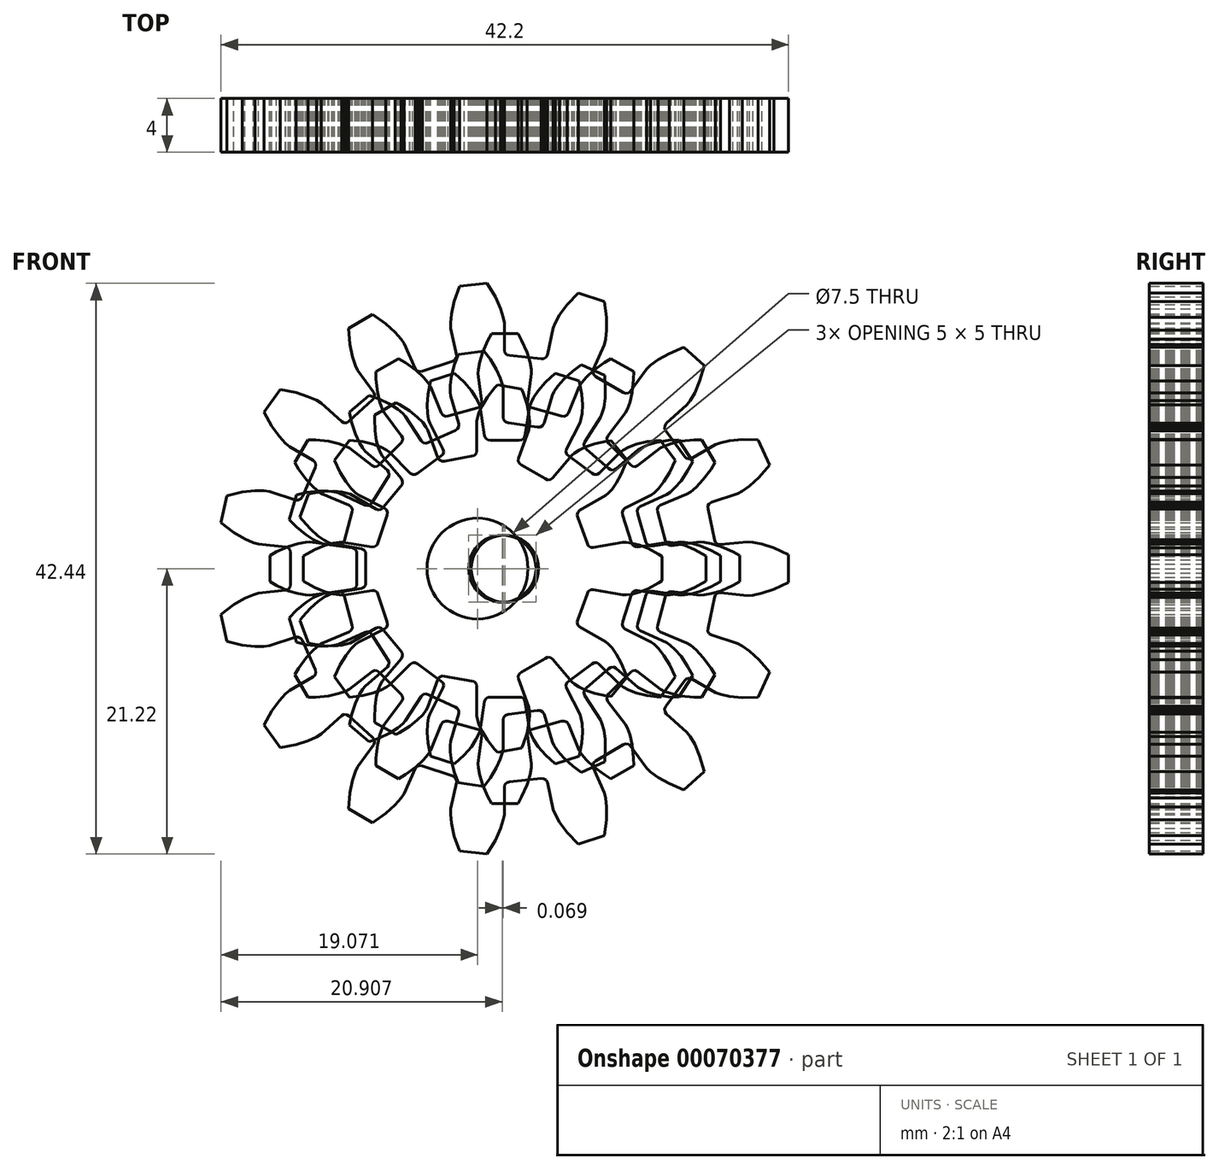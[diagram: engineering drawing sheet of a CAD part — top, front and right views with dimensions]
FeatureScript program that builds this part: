
annotation { "Feature Type Name" : "Feature", "Feature Type Description" : "" }
export const myFeature = defineFeature(function(context is Context, id is Id, definition is map)
    precondition{}
    {
        {
            var Q0;
            Q0=qCreatedBy(makeId("Front.planeOp"),FACE);
            var sketch = newSketch(context, id + "F0", { "sketchPlane" : qUnion([Q0])});
            skLineSegment(sketch, "E0", {"start": v(9.06, -8.12) * mm, "end": v(8.97, -7.83) * mm});
            skLineSegment(sketch, "E1", {"start": v(8.97, -7.83) * mm, "end": v(8.64, -7) * mm});
            skLineSegment(sketch, "E2", {"start": v(8.64, -7) * mm, "end": v(8.3, -6.36) * mm});
            skLineSegment(sketch, "E3", {"start": v(8.3, -6.36) * mm, "end": v(7.96, -5.9) * mm});
            skLineSegment(sketch, "E4", {"start": v(7.96, -5.9) * mm, "end": v(7.69, -5.6) * mm});
            skLineSegment(sketch, "E5", {"start": v(7.69, -5.6) * mm, "end": v(7.5, -5.44) * mm});
            skLineSegment(sketch, "E6", {"start": v(7.5, -5.44) * mm, "end": v(5.57, -4.33) * mm});
            skLineSegment(sketch, "E7", {"start": v(5.57, -4.33) * mm, "end": v(5.43, -4.2) * mm});
            skLineSegment(sketch, "E8", {"start": v(5.43, -4.2) * mm, "end": v(5.37, -4) * mm});
            skLineSegment(sketch, "E9", {"start": v(5.37, -4) * mm, "end": v(5.43, -3.8) * mm});
            skLineSegment(sketch, "E10", {"start": v(5.43, -3.8) * mm, "end": v(6.12, -1.88) * mm});
            skLineSegment(sketch, "E11", {"start": v(6.12, -1.88) * mm, "end": v(6.2, -1.7) * mm});
            skLineSegment(sketch, "E12", {"start": v(6.2, -1.7) * mm, "end": v(6.38, -1.58) * mm});
            skLineSegment(sketch, "E13", {"start": v(6.38, -1.58) * mm, "end": v(6.58, -1.57) * mm});
            skLineSegment(sketch, "E14", {"start": v(6.58, -1.57) * mm, "end": v(8.77, -1.96) * mm});
            skLineSegment(sketch, "E15", {"start": v(8.77, -1.96) * mm, "end": v(9.01, -1.96) * mm});
            skLineSegment(sketch, "E16", {"start": v(9.01, -1.96) * mm, "end": v(9.41, -1.9) * mm});
            skLineSegment(sketch, "E17", {"start": v(9.41, -1.9) * mm, "end": v(9.96, -1.76) * mm});
            skLineSegment(sketch, "E18", {"start": v(9.96, -1.76) * mm, "end": v(10.65, -1.5) * mm});
            skLineSegment(sketch, "E19", {"start": v(10.65, -1.5) * mm, "end": v(11.43, -1.07) * mm});
            skLineSegment(sketch, "E20", {"start": v(11.43, -1.07) * mm, "end": v(11.7, -0.9) * mm});
            skLineSegment(sketch, "E21", {"start": v(11.7, -0.9) * mm, "end": v(11.7, 0.9) * mm});
            skLineSegment(sketch, "E22", {"start": v(11.7, 0.9) * mm, "end": v(11.43, 1.07) * mm});
            skLineSegment(sketch, "E23", {"start": v(11.43, 1.07) * mm, "end": v(10.65, 1.5) * mm});
            skLineSegment(sketch, "E24", {"start": v(10.65, 1.5) * mm, "end": v(9.96, 1.76) * mm});
            skLineSegment(sketch, "E25", {"start": v(9.96, 1.76) * mm, "end": v(9.41, 1.9) * mm});
            skLineSegment(sketch, "E26", {"start": v(9.41, 1.9) * mm, "end": v(9.01, 1.96) * mm});
            skLineSegment(sketch, "E27", {"start": v(9.01, 1.96) * mm, "end": v(8.77, 1.96) * mm});
            skLineSegment(sketch, "E28", {"start": v(8.77, 1.96) * mm, "end": v(6.58, 1.57) * mm});
            skLineSegment(sketch, "E29", {"start": v(6.58, 1.57) * mm, "end": v(6.38, 1.58) * mm});
            skLineSegment(sketch, "E30", {"start": v(6.38, 1.58) * mm, "end": v(6.2, 1.7) * mm});
            skLineSegment(sketch, "E31", {"start": v(6.2, 1.7) * mm, "end": v(6.12, 1.88) * mm});
            skLineSegment(sketch, "E32", {"start": v(6.12, 1.88) * mm, "end": v(5.43, 3.8) * mm});
            skLineSegment(sketch, "E33", {"start": v(5.43, 3.8) * mm, "end": v(5.37, 4) * mm});
            skLineSegment(sketch, "E34", {"start": v(5.37, 4) * mm, "end": v(5.43, 4.2) * mm});
            skLineSegment(sketch, "E35", {"start": v(5.43, 4.2) * mm, "end": v(5.57, 4.33) * mm});
            skLineSegment(sketch, "E36", {"start": v(5.57, 4.33) * mm, "end": v(7.5, 5.44) * mm});
            skLineSegment(sketch, "E37", {"start": v(7.5, 5.44) * mm, "end": v(7.69, 5.6) * mm});
            skLineSegment(sketch, "E38", {"start": v(7.69, 5.6) * mm, "end": v(7.96, 5.9) * mm});
            skLineSegment(sketch, "E39", {"start": v(7.96, 5.9) * mm, "end": v(8.3, 6.36) * mm});
            skLineSegment(sketch, "E40", {"start": v(8.3, 6.36) * mm, "end": v(8.64, 7) * mm});
            skLineSegment(sketch, "E41", {"start": v(8.64, 7) * mm, "end": v(8.97, 7.83) * mm});
            skLineSegment(sketch, "E42", {"start": v(8.97, 7.83) * mm, "end": v(9.06, 8.12) * mm});
            skLineSegment(sketch, "E43", {"start": v(9.06, 8.12) * mm, "end": v(7.9, 9.51) * mm});
            skLineSegment(sketch, "E44", {"start": v(7.9, 9.51) * mm, "end": v(7.6, 9.48) * mm});
            skLineSegment(sketch, "E45", {"start": v(7.6, 9.48) * mm, "end": v(6.72, 9.3) * mm});
            skLineSegment(sketch, "E46", {"start": v(6.72, 9.3) * mm, "end": v(6.03, 9.06) * mm});
            skLineSegment(sketch, "E47", {"start": v(6.03, 9.06) * mm, "end": v(5.51, 8.81) * mm});
            skLineSegment(sketch, "E48", {"start": v(5.51, 8.81) * mm, "end": v(5.17, 8.6) * mm});
            skLineSegment(sketch, "E49", {"start": v(5.17, 8.6) * mm, "end": v(4.98, 8.44) * mm});
            skLineSegment(sketch, "E50", {"start": v(4.98, 8.44) * mm, "end": v(3.56, 6.73) * mm});
            skLineSegment(sketch, "E51", {"start": v(3.56, 6.73) * mm, "end": v(3.4, 6.62) * mm});
            skLineSegment(sketch, "E52", {"start": v(3.4, 6.62) * mm, "end": v(3.19, 6.6) * mm});
            skLineSegment(sketch, "E53", {"start": v(3.19, 6.6) * mm, "end": v(3, 6.68) * mm});
            skLineSegment(sketch, "E54", {"start": v(3, 6.68) * mm, "end": v(1.24, 7.7) * mm});
            skLineSegment(sketch, "E55", {"start": v(1.24, 7.7) * mm, "end": v(1.07, 7.82) * mm});
            skLineSegment(sketch, "E56", {"start": v(1.07, 7.82) * mm, "end": v(0.99, 8) * mm});
            skLineSegment(sketch, "E57", {"start": v(0.99, 8) * mm, "end": v(1, 8.2) * mm});
            skLineSegment(sketch, "E58", {"start": v(1, 8.2) * mm, "end": v(1.77, 10.3) * mm});
            skLineSegment(sketch, "E59", {"start": v(1.77, 10.3) * mm, "end": v(1.81, 10.53) * mm});
            skLineSegment(sketch, "E60", {"start": v(1.81, 10.53) * mm, "end": v(1.83, 10.94) * mm});
            skLineSegment(sketch, "E61", {"start": v(1.83, 10.94) * mm, "end": v(1.79, 11.5) * mm});
            skLineSegment(sketch, "E62", {"start": v(1.79, 11.5) * mm, "end": v(1.65, 12.22) * mm});
            skLineSegment(sketch, "E63", {"start": v(1.65, 12.22) * mm, "end": v(1.37, 13.07) * mm});
            skLineSegment(sketch, "E64", {"start": v(1.37, 13.07) * mm, "end": v(1.25, 13.35) * mm});
            skLineSegment(sketch, "E65", {"start": v(1.25, 13.35) * mm, "end": v(-0.54, 13.67) * mm});
            skLineSegment(sketch, "E66", {"start": v(-0.54, 13.67) * mm, "end": v(-0.75, 13.44) * mm});
            skLineSegment(sketch, "E67", {"start": v(-0.75, 13.44) * mm, "end": v(-1.3, 12.74) * mm});
            skLineSegment(sketch, "E68", {"start": v(-1.3, 12.74) * mm, "end": v(-1.68, 12.12) * mm});
            skLineSegment(sketch, "E69", {"start": v(-1.68, 12.12) * mm, "end": v(-1.92, 11.6) * mm});
            skLineSegment(sketch, "E70", {"start": v(-1.92, 11.6) * mm, "end": v(-2.04, 11.21) * mm});
            skLineSegment(sketch, "E71", {"start": v(-2.04, 11.21) * mm, "end": v(-2.08, 10.97) * mm});
            skLineSegment(sketch, "E72", {"start": v(-2.08, 10.97) * mm, "end": v(-2.08, 8.75) * mm});
            skLineSegment(sketch, "E73", {"start": v(-2.08, 8.75) * mm, "end": v(-2.13, 8.55) * mm});
            skLineSegment(sketch, "E74", {"start": v(-2.13, 8.55) * mm, "end": v(-2.27, 8.4) * mm});
            skLineSegment(sketch, "E75", {"start": v(-2.27, 8.4) * mm, "end": v(-2.47, 8.36) * mm});
            skLineSegment(sketch, "E76", {"start": v(-2.47, 8.36) * mm, "end": v(-4.47, 8) * mm});
            skLineSegment(sketch, "E77", {"start": v(-4.47, 8) * mm, "end": v(-4.68, 7.98) * mm});
            skLineSegment(sketch, "E78", {"start": v(-4.68, 7.98) * mm, "end": v(-4.86, 8.07) * mm});
            skLineSegment(sketch, "E79", {"start": v(-4.86, 8.07) * mm, "end": v(-4.98, 8.24) * mm});
            skLineSegment(sketch, "E80", {"start": v(-4.98, 8.24) * mm, "end": v(-5.73, 10.33) * mm});
            skLineSegment(sketch, "E81", {"start": v(-5.73, 10.33) * mm, "end": v(-5.86, 10.54) * mm});
            skLineSegment(sketch, "E82", {"start": v(-5.86, 10.54) * mm, "end": v(-6.1, 10.86) * mm});
            skLineSegment(sketch, "E83", {"start": v(-6.1, 10.86) * mm, "end": v(-6.5, 11.27) * mm});
            skLineSegment(sketch, "E84", {"start": v(-6.5, 11.27) * mm, "end": v(-7.07, 11.73) * mm});
            skLineSegment(sketch, "E85", {"start": v(-7.07, 11.73) * mm, "end": v(-7.83, 12.2) * mm});
            skLineSegment(sketch, "E86", {"start": v(-7.83, 12.2) * mm, "end": v(-8.1, 12.34) * mm});
            skLineSegment(sketch, "E87", {"start": v(-8.1, 12.34) * mm, "end": v(-9.68, 11.43) * mm});
            skLineSegment(sketch, "E88", {"start": v(-9.68, 11.43) * mm, "end": v(-9.7, 11.12) * mm});
            skLineSegment(sketch, "E89", {"start": v(-9.7, 11.12) * mm, "end": v(-9.66, 10.23) * mm});
            skLineSegment(sketch, "E90", {"start": v(-9.66, 10.23) * mm, "end": v(-9.55, 9.5) * mm});
            skLineSegment(sketch, "E91", {"start": v(-9.55, 9.5) * mm, "end": v(-9.4, 8.96) * mm});
            skLineSegment(sketch, "E92", {"start": v(-9.4, 8.96) * mm, "end": v(-9.24, 8.58) * mm});
            skLineSegment(sketch, "E93", {"start": v(-9.24, 8.58) * mm, "end": v(-9.12, 8.37) * mm});
            skLineSegment(sketch, "E94", {"start": v(-9.12, 8.37) * mm, "end": v(-7.7, 6.67) * mm});
            skLineSegment(sketch, "E95", {"start": v(-7.7, 6.67) * mm, "end": v(-7.6, 6.49) * mm});
            skLineSegment(sketch, "E96", {"start": v(-7.6, 6.49) * mm, "end": v(-7.62, 6.29) * mm});
            skLineSegment(sketch, "E97", {"start": v(-7.62, 6.29) * mm, "end": v(-7.74, 6.12) * mm});
            skLineSegment(sketch, "E98", {"start": v(-7.74, 6.12) * mm, "end": v(-9.05, 4.56) * mm});
            skLineSegment(sketch, "E99", {"start": v(-9.05, 4.56) * mm, "end": v(-9.2, 4.41) * mm});
            skLineSegment(sketch, "E100", {"start": v(-9.2, 4.41) * mm, "end": v(-9.39, 4.36) * mm});
            skLineSegment(sketch, "E101", {"start": v(-9.39, 4.36) * mm, "end": v(-9.58, 4.42) * mm});
            skLineSegment(sketch, "E102", {"start": v(-9.58, 4.42) * mm, "end": v(-11.5, 5.53) * mm});
            skLineSegment(sketch, "E103", {"start": v(-11.5, 5.53) * mm, "end": v(-11.73, 5.61) * mm});
            skLineSegment(sketch, "E104", {"start": v(-11.73, 5.61) * mm, "end": v(-12.13, 5.7) * mm});
            skLineSegment(sketch, "E105", {"start": v(-12.13, 5.7) * mm, "end": v(-12.7, 5.76) * mm});
            skLineSegment(sketch, "E106", {"start": v(-12.7, 5.76) * mm, "end": v(-13.43, 5.74) * mm});
            skLineSegment(sketch, "E107", {"start": v(-13.43, 5.74) * mm, "end": v(-14.31, 5.61) * mm});
            skLineSegment(sketch, "E108", {"start": v(-14.31, 5.61) * mm, "end": v(-14.61, 5.55) * mm});
            skLineSegment(sketch, "E109", {"start": v(-14.61, 5.55) * mm, "end": v(-15.23, 3.84) * mm});
            skLineSegment(sketch, "E110", {"start": v(-15.23, 3.84) * mm, "end": v(-15.05, 3.6) * mm});
            skLineSegment(sketch, "E111", {"start": v(-15.05, 3.6) * mm, "end": v(-14.45, 2.93) * mm});
            skLineSegment(sketch, "E112", {"start": v(-14.45, 2.93) * mm, "end": v(-13.9, 2.45) * mm});
            skLineSegment(sketch, "E113", {"start": v(-13.9, 2.45) * mm, "end": v(-13.43, 2.12) * mm});
            skLineSegment(sketch, "E114", {"start": v(-13.43, 2.12) * mm, "end": v(-13.07, 1.94) * mm});
            skLineSegment(sketch, "E115", {"start": v(-13.07, 1.94) * mm, "end": v(-12.84, 1.85) * mm});
            skLineSegment(sketch, "E116", {"start": v(-12.84, 1.85) * mm, "end": v(-10.65, 1.47) * mm});
            skLineSegment(sketch, "E117", {"start": v(-10.65, 1.47) * mm, "end": v(-10.47, 1.39) * mm});
            skLineSegment(sketch, "E118", {"start": v(-10.47, 1.39) * mm, "end": v(-10.35, 1.22) * mm});
            skLineSegment(sketch, "E119", {"start": v(-10.35, 1.22) * mm, "end": v(-10.33, 1.02) * mm});
            skLineSegment(sketch, "E120", {"start": v(-10.33, 1.02) * mm, "end": v(-10.33, -1.02) * mm});
            skLineSegment(sketch, "E121", {"start": v(-10.33, -1.02) * mm, "end": v(-10.35, -1.22) * mm});
            skLineSegment(sketch, "E122", {"start": v(-10.35, -1.22) * mm, "end": v(-10.47, -1.39) * mm});
            skLineSegment(sketch, "E123", {"start": v(-10.47, -1.39) * mm, "end": v(-10.65, -1.47) * mm});
            skLineSegment(sketch, "E124", {"start": v(-10.65, -1.47) * mm, "end": v(-12.84, -1.85) * mm});
            skLineSegment(sketch, "E125", {"start": v(-12.84, -1.85) * mm, "end": v(-13.07, -1.94) * mm});
            skLineSegment(sketch, "E126", {"start": v(-13.07, -1.94) * mm, "end": v(-13.43, -2.12) * mm});
            skLineSegment(sketch, "E127", {"start": v(-13.43, -2.12) * mm, "end": v(-13.9, -2.45) * mm});
            skLineSegment(sketch, "E128", {"start": v(-13.9, -2.45) * mm, "end": v(-14.45, -2.93) * mm});
            skLineSegment(sketch, "E129", {"start": v(-14.45, -2.93) * mm, "end": v(-15.05, -3.6) * mm});
            skLineSegment(sketch, "E130", {"start": v(-15.05, -3.6) * mm, "end": v(-15.23, -3.84) * mm});
            skLineSegment(sketch, "E131", {"start": v(-15.23, -3.84) * mm, "end": v(-14.61, -5.55) * mm});
            skLineSegment(sketch, "E132", {"start": v(-14.61, -5.55) * mm, "end": v(-14.31, -5.61) * mm});
            skLineSegment(sketch, "E133", {"start": v(-14.31, -5.61) * mm, "end": v(-13.43, -5.74) * mm});
            skLineSegment(sketch, "E134", {"start": v(-13.43, -5.74) * mm, "end": v(-12.7, -5.76) * mm});
            skLineSegment(sketch, "E135", {"start": v(-12.7, -5.76) * mm, "end": v(-12.13, -5.7) * mm});
            skLineSegment(sketch, "E136", {"start": v(-12.13, -5.7) * mm, "end": v(-11.73, -5.61) * mm});
            skLineSegment(sketch, "E137", {"start": v(-11.73, -5.61) * mm, "end": v(-11.5, -5.53) * mm});
            skLineSegment(sketch, "E138", {"start": v(-11.5, -5.53) * mm, "end": v(-9.58, -4.42) * mm});
            skLineSegment(sketch, "E139", {"start": v(-9.58, -4.42) * mm, "end": v(-9.39, -4.36) * mm});
            skLineSegment(sketch, "E140", {"start": v(-9.39, -4.36) * mm, "end": v(-9.2, -4.41) * mm});
            skLineSegment(sketch, "E141", {"start": v(-9.2, -4.41) * mm, "end": v(-9.05, -4.56) * mm});
            skLineSegment(sketch, "E142", {"start": v(-9.05, -4.56) * mm, "end": v(-7.74, -6.12) * mm});
            skLineSegment(sketch, "E143", {"start": v(-7.74, -6.12) * mm, "end": v(-7.62, -6.29) * mm});
            skLineSegment(sketch, "E144", {"start": v(-7.62, -6.29) * mm, "end": v(-7.6, -6.49) * mm});
            skLineSegment(sketch, "E145", {"start": v(-7.6, -6.49) * mm, "end": v(-7.7, -6.67) * mm});
            skLineSegment(sketch, "E146", {"start": v(-7.7, -6.67) * mm, "end": v(-9.12, -8.37) * mm});
            skLineSegment(sketch, "E147", {"start": v(-9.12, -8.37) * mm, "end": v(-9.24, -8.58) * mm});
            skLineSegment(sketch, "E148", {"start": v(-9.24, -8.58) * mm, "end": v(-9.4, -8.96) * mm});
            skLineSegment(sketch, "E149", {"start": v(-9.4, -8.96) * mm, "end": v(-9.55, -9.5) * mm});
            skLineSegment(sketch, "E150", {"start": v(-9.55, -9.5) * mm, "end": v(-9.66, -10.23) * mm});
            skLineSegment(sketch, "E151", {"start": v(-9.66, -10.23) * mm, "end": v(-9.7, -11.12) * mm});
            skLineSegment(sketch, "E152", {"start": v(-9.7, -11.12) * mm, "end": v(-9.68, -11.43) * mm});
            skLineSegment(sketch, "E153", {"start": v(-9.68, -11.43) * mm, "end": v(-8.1, -12.34) * mm});
            skLineSegment(sketch, "E154", {"start": v(-8.1, -12.34) * mm, "end": v(-7.83, -12.2) * mm});
            skLineSegment(sketch, "E155", {"start": v(-7.83, -12.2) * mm, "end": v(-7.07, -11.73) * mm});
            skLineSegment(sketch, "E156", {"start": v(-7.07, -11.73) * mm, "end": v(-6.5, -11.27) * mm});
            skLineSegment(sketch, "E157", {"start": v(-6.5, -11.27) * mm, "end": v(-6.1, -10.86) * mm});
            skLineSegment(sketch, "E158", {"start": v(-6.1, -10.86) * mm, "end": v(-5.86, -10.54) * mm});
            skLineSegment(sketch, "E159", {"start": v(-5.86, -10.54) * mm, "end": v(-5.73, -10.33) * mm});
            skLineSegment(sketch, "E160", {"start": v(-5.73, -10.33) * mm, "end": v(-4.98, -8.24) * mm});
            skLineSegment(sketch, "E161", {"start": v(-4.98, -8.24) * mm, "end": v(-4.86, -8.07) * mm});
            skLineSegment(sketch, "E162", {"start": v(-4.86, -8.07) * mm, "end": v(-4.68, -7.98) * mm});
            skLineSegment(sketch, "E163", {"start": v(-4.68, -7.98) * mm, "end": v(-4.47, -8) * mm});
            skLineSegment(sketch, "E164", {"start": v(-4.47, -8) * mm, "end": v(-2.47, -8.36) * mm});
            skLineSegment(sketch, "E165", {"start": v(-2.47, -8.36) * mm, "end": v(-2.27, -8.4) * mm});
            skLineSegment(sketch, "E166", {"start": v(-2.27, -8.4) * mm, "end": v(-2.13, -8.55) * mm});
            skLineSegment(sketch, "E167", {"start": v(-2.13, -8.55) * mm, "end": v(-2.08, -8.75) * mm});
            skLineSegment(sketch, "E168", {"start": v(-2.08, -8.75) * mm, "end": v(-2.08, -10.97) * mm});
            skLineSegment(sketch, "E169", {"start": v(-2.08, -10.97) * mm, "end": v(-2.04, -11.21) * mm});
            skLineSegment(sketch, "E170", {"start": v(-2.04, -11.21) * mm, "end": v(-1.92, -11.6) * mm});
            skLineSegment(sketch, "E171", {"start": v(-1.92, -11.6) * mm, "end": v(-1.68, -12.12) * mm});
            skLineSegment(sketch, "E172", {"start": v(-1.68, -12.12) * mm, "end": v(-1.3, -12.74) * mm});
            skLineSegment(sketch, "E173", {"start": v(-1.3, -12.74) * mm, "end": v(-0.75, -13.44) * mm});
            skLineSegment(sketch, "E174", {"start": v(-0.75, -13.44) * mm, "end": v(-0.54, -13.67) * mm});
            skLineSegment(sketch, "E175", {"start": v(-0.54, -13.67) * mm, "end": v(1.25, -13.35) * mm});
            skLineSegment(sketch, "E176", {"start": v(1.25, -13.35) * mm, "end": v(1.37, -13.07) * mm});
            skLineSegment(sketch, "E177", {"start": v(1.37, -13.07) * mm, "end": v(1.65, -12.22) * mm});
            skLineSegment(sketch, "E178", {"start": v(1.65, -12.22) * mm, "end": v(1.79, -11.5) * mm});
            skLineSegment(sketch, "E179", {"start": v(1.79, -11.5) * mm, "end": v(1.83, -10.94) * mm});
            skLineSegment(sketch, "E180", {"start": v(1.83, -10.94) * mm, "end": v(1.81, -10.53) * mm});
            skLineSegment(sketch, "E181", {"start": v(1.81, -10.53) * mm, "end": v(1.77, -10.3) * mm});
            skLineSegment(sketch, "E182", {"start": v(1.77, -10.3) * mm, "end": v(1, -8.2) * mm});
            skLineSegment(sketch, "E183", {"start": v(1, -8.2) * mm, "end": v(0.99, -8) * mm});
            skLineSegment(sketch, "E184", {"start": v(0.99, -8) * mm, "end": v(1.07, -7.82) * mm});
            skLineSegment(sketch, "E185", {"start": v(1.07, -7.82) * mm, "end": v(1.24, -7.7) * mm});
            skLineSegment(sketch, "E186", {"start": v(1.24, -7.7) * mm, "end": v(3, -6.68) * mm});
            skLineSegment(sketch, "E187", {"start": v(3, -6.68) * mm, "end": v(3.19, -6.6) * mm});
            skLineSegment(sketch, "E188", {"start": v(3.19, -6.6) * mm, "end": v(3.4, -6.62) * mm});
            skLineSegment(sketch, "E189", {"start": v(3.4, -6.62) * mm, "end": v(3.56, -6.73) * mm});
            skLineSegment(sketch, "E190", {"start": v(3.56, -6.73) * mm, "end": v(4.98, -8.44) * mm});
            skLineSegment(sketch, "E191", {"start": v(4.98, -8.44) * mm, "end": v(5.17, -8.6) * mm});
            skLineSegment(sketch, "E192", {"start": v(5.17, -8.6) * mm, "end": v(5.51, -8.81) * mm});
            skLineSegment(sketch, "E193", {"start": v(5.51, -8.81) * mm, "end": v(6.03, -9.06) * mm});
            skLineSegment(sketch, "E194", {"start": v(6.03, -9.06) * mm, "end": v(6.72, -9.3) * mm});
            skLineSegment(sketch, "E195", {"start": v(6.72, -9.3) * mm, "end": v(7.6, -9.48) * mm});
            skLineSegment(sketch, "E196", {"start": v(7.6, -9.48) * mm, "end": v(7.9, -9.51) * mm});
            skLineSegment(sketch, "E197", {"start": v(7.9, -9.51) * mm, "end": v(9.06, -8.12) * mm});
            skCircle(sketch, "E198", {"center": v(-2.03, 0) * mm, "radius": 3.75 * mm});
            skCircle(sketch, "E199", {"center": v(-2.03, 0) * mm, "radius": 1.25 * mm});
            skSolve(sketch);
        }
        {
            var Q0;
            Q0=makeQuery(id+"F0.imprint","IMPRINT",FACE,{"disambiguationData":[TD([[makeQuery(id+"F0.imprint","IMPRINT",EDGE,{"derivedFrom":sQuery(id+"F0.wireOp",EDGE,"E0")}),1.0]])]});
            extrude(context, id + "F1", {"entities" : qUnion([Q0]), "depth" : 4 * mm});
        }
        {
            var Q0;
            Q0=qCreatedBy(makeId("Front.planeOp"),FACE);
            var sketch = newSketch(context, id + "F2", { "sketchPlane" : qUnion([Q0])});
            skLineSegment(sketch, "E200", {"start": v(12.66, -8.04) * mm, "end": v(12.25, -7.15) * mm});
            skLineSegment(sketch, "E201", {"start": v(12.25, -7.15) * mm, "end": v(11.82, -6.46) * mm});
            skLineSegment(sketch, "E202", {"start": v(11.82, -6.46) * mm, "end": v(11.43, -5.96) * mm});
            skLineSegment(sketch, "E203", {"start": v(11.43, -5.96) * mm, "end": v(11.1, -5.65) * mm});
            skLineSegment(sketch, "E204", {"start": v(11.1, -5.65) * mm, "end": v(10.9, -5.48) * mm});
            skLineSegment(sketch, "E205", {"start": v(10.9, -5.48) * mm, "end": v(8.94, -4.5) * mm});
            skLineSegment(sketch, "E206", {"start": v(8.94, -4.5) * mm, "end": v(8.78, -4.36) * mm});
            skLineSegment(sketch, "E207", {"start": v(8.78, -4.36) * mm, "end": v(8.72, -4.16) * mm});
            skLineSegment(sketch, "E208", {"start": v(8.72, -4.16) * mm, "end": v(8.76, -3.96) * mm});
            skLineSegment(sketch, "E209", {"start": v(8.76, -3.96) * mm, "end": v(9.42, -1.94) * mm});
            skLineSegment(sketch, "E210", {"start": v(9.42, -1.94) * mm, "end": v(9.5, -1.76) * mm});
            skLineSegment(sketch, "E211", {"start": v(9.5, -1.76) * mm, "end": v(9.67, -1.64) * mm});
            skLineSegment(sketch, "E212", {"start": v(9.67, -1.64) * mm, "end": v(9.87, -1.62) * mm});
            skLineSegment(sketch, "E213", {"start": v(9.87, -1.62) * mm, "end": v(12.03, -1.97) * mm});
            skLineSegment(sketch, "E214", {"start": v(12.03, -1.97) * mm, "end": v(12.3, -1.96) * mm});
            skLineSegment(sketch, "E215", {"start": v(12.3, -1.96) * mm, "end": v(12.75, -1.9) * mm});
            skLineSegment(sketch, "E216", {"start": v(12.75, -1.9) * mm, "end": v(13.36, -1.73) * mm});
            skLineSegment(sketch, "E217", {"start": v(13.36, -1.73) * mm, "end": v(14.11, -1.42) * mm});
            skLineSegment(sketch, "E218", {"start": v(14.11, -1.42) * mm, "end": v(14.97, -0.94) * mm});
            skLineSegment(sketch, "E219", {"start": v(14.97, -0.94) * mm, "end": v(14.97, 0.94) * mm});
            skLineSegment(sketch, "E220", {"start": v(14.97, 0.94) * mm, "end": v(14.11, 1.42) * mm});
            skLineSegment(sketch, "E221", {"start": v(14.11, 1.42) * mm, "end": v(13.36, 1.73) * mm});
            skLineSegment(sketch, "E222", {"start": v(13.36, 1.73) * mm, "end": v(12.75, 1.9) * mm});
            skLineSegment(sketch, "E223", {"start": v(12.75, 1.9) * mm, "end": v(12.3, 1.96) * mm});
            skLineSegment(sketch, "E224", {"start": v(12.3, 1.96) * mm, "end": v(12.03, 1.97) * mm});
            skLineSegment(sketch, "E225", {"start": v(12.03, 1.97) * mm, "end": v(9.87, 1.62) * mm});
            skLineSegment(sketch, "E226", {"start": v(9.87, 1.62) * mm, "end": v(9.67, 1.64) * mm});
            skLineSegment(sketch, "E227", {"start": v(9.67, 1.64) * mm, "end": v(9.5, 1.76) * mm});
            skLineSegment(sketch, "E228", {"start": v(9.5, 1.76) * mm, "end": v(9.42, 1.94) * mm});
            skLineSegment(sketch, "E229", {"start": v(9.42, 1.94) * mm, "end": v(8.76, 3.96) * mm});
            skLineSegment(sketch, "E230", {"start": v(8.76, 3.96) * mm, "end": v(8.72, 4.16) * mm});
            skLineSegment(sketch, "E231", {"start": v(8.72, 4.16) * mm, "end": v(8.78, 4.36) * mm});
            skLineSegment(sketch, "E232", {"start": v(8.78, 4.36) * mm, "end": v(8.94, 4.5) * mm});
            skLineSegment(sketch, "E233", {"start": v(8.94, 4.5) * mm, "end": v(10.9, 5.48) * mm});
            skLineSegment(sketch, "E234", {"start": v(10.9, 5.48) * mm, "end": v(11.1, 5.65) * mm});
            skLineSegment(sketch, "E235", {"start": v(11.1, 5.65) * mm, "end": v(11.43, 5.96) * mm});
            skLineSegment(sketch, "E236", {"start": v(11.43, 5.96) * mm, "end": v(11.82, 6.46) * mm});
            skLineSegment(sketch, "E237", {"start": v(11.82, 6.46) * mm, "end": v(12.25, 7.15) * mm});
            skLineSegment(sketch, "E238", {"start": v(12.25, 7.15) * mm, "end": v(12.66, 8.04) * mm});
            skLineSegment(sketch, "E239", {"start": v(12.66, 8.04) * mm, "end": v(11.56, 9.56) * mm});
            skLineSegment(sketch, "E240", {"start": v(11.56, 9.56) * mm, "end": v(10.58, 9.44) * mm});
            skLineSegment(sketch, "E241", {"start": v(10.58, 9.44) * mm, "end": v(9.8, 9.25) * mm});
            skLineSegment(sketch, "E242", {"start": v(9.8, 9.25) * mm, "end": v(9.2, 9.03) * mm});
            skLineSegment(sketch, "E243", {"start": v(9.2, 9.03) * mm, "end": v(8.8, 8.82) * mm});
            skLineSegment(sketch, "E244", {"start": v(8.8, 8.82) * mm, "end": v(8.58, 8.66) * mm});
            skLineSegment(sketch, "E245", {"start": v(8.58, 8.66) * mm, "end": v(7.03, 7.11) * mm});
            skLineSegment(sketch, "E246", {"start": v(7.03, 7.11) * mm, "end": v(6.86, 7) * mm});
            skLineSegment(sketch, "E247", {"start": v(6.86, 7) * mm, "end": v(6.65, 7) * mm});
            skLineSegment(sketch, "E248", {"start": v(6.65, 7) * mm, "end": v(6.48, 7.1) * mm});
            skLineSegment(sketch, "E249", {"start": v(6.48, 7.1) * mm, "end": v(4.76, 8.36) * mm});
            skLineSegment(sketch, "E250", {"start": v(4.76, 8.36) * mm, "end": v(4.6, 8.5) * mm});
            skLineSegment(sketch, "E251", {"start": v(4.6, 8.5) * mm, "end": v(4.55, 8.69) * mm});
            skLineSegment(sketch, "E252", {"start": v(4.55, 8.69) * mm, "end": v(4.59, 8.88) * mm});
            skLineSegment(sketch, "E253", {"start": v(4.59, 8.88) * mm, "end": v(5.59, 10.84) * mm});
            skLineSegment(sketch, "E254", {"start": v(5.59, 10.84) * mm, "end": v(5.67, 11.1) * mm});
            skLineSegment(sketch, "E255", {"start": v(5.67, 11.1) * mm, "end": v(5.74, 11.54) * mm});
            skLineSegment(sketch, "E256", {"start": v(5.74, 11.54) * mm, "end": v(5.77, 12.17) * mm});
            skLineSegment(sketch, "E257", {"start": v(5.77, 12.17) * mm, "end": v(5.7, 12.98) * mm});
            skLineSegment(sketch, "E258", {"start": v(5.7, 12.98) * mm, "end": v(5.52, 13.95) * mm});
            skLineSegment(sketch, "E259", {"start": v(5.52, 13.95) * mm, "end": v(3.74, 14.53) * mm});
            skLineSegment(sketch, "E260", {"start": v(3.74, 14.53) * mm, "end": v(3.01, 13.86) * mm});
            skLineSegment(sketch, "E261", {"start": v(3.01, 13.86) * mm, "end": v(2.49, 13.24) * mm});
            skLineSegment(sketch, "E262", {"start": v(2.49, 13.24) * mm, "end": v(2.14, 12.71) * mm});
            skLineSegment(sketch, "E263", {"start": v(2.14, 12.71) * mm, "end": v(1.94, 12.3) * mm});
            skLineSegment(sketch, "E264", {"start": v(1.94, 12.3) * mm, "end": v(1.85, 12.05) * mm});
            skLineSegment(sketch, "E265", {"start": v(1.85, 12.05) * mm, "end": v(1.5, 9.89) * mm});
            skLineSegment(sketch, "E266", {"start": v(1.5, 9.89) * mm, "end": v(1.43, 9.7) * mm});
            skLineSegment(sketch, "E267", {"start": v(1.43, 9.7) * mm, "end": v(1.26, 9.58) * mm});
            skLineSegment(sketch, "E268", {"start": v(1.26, 9.58) * mm, "end": v(1.06, 9.56) * mm});
            skLineSegment(sketch, "E269", {"start": v(1.06, 9.56) * mm, "end": v(-1.06, 9.56) * mm});
            skLineSegment(sketch, "E270", {"start": v(-1.06, 9.56) * mm, "end": v(-1.26, 9.58) * mm});
            skLineSegment(sketch, "E271", {"start": v(-1.26, 9.58) * mm, "end": v(-1.43, 9.7) * mm});
            skLineSegment(sketch, "E272", {"start": v(-1.43, 9.7) * mm, "end": v(-1.5, 9.89) * mm});
            skLineSegment(sketch, "E273", {"start": v(-1.5, 9.89) * mm, "end": v(-1.85, 12.05) * mm});
            skLineSegment(sketch, "E274", {"start": v(-1.85, 12.05) * mm, "end": v(-1.94, 12.3) * mm});
            skLineSegment(sketch, "E275", {"start": v(-1.94, 12.3) * mm, "end": v(-2.14, 12.71) * mm});
            skLineSegment(sketch, "E276", {"start": v(-2.14, 12.71) * mm, "end": v(-2.49, 13.24) * mm});
            skLineSegment(sketch, "E277", {"start": v(-2.49, 13.24) * mm, "end": v(-3.01, 13.86) * mm});
            skLineSegment(sketch, "E278", {"start": v(-3.01, 13.86) * mm, "end": v(-3.74, 14.53) * mm});
            skLineSegment(sketch, "E279", {"start": v(-3.74, 14.53) * mm, "end": v(-5.52, 13.95) * mm});
            skLineSegment(sketch, "E280", {"start": v(-5.52, 13.95) * mm, "end": v(-5.7, 12.98) * mm});
            skLineSegment(sketch, "E281", {"start": v(-5.7, 12.98) * mm, "end": v(-5.77, 12.17) * mm});
            skLineSegment(sketch, "E282", {"start": v(-5.77, 12.17) * mm, "end": v(-5.74, 11.54) * mm});
            skLineSegment(sketch, "E283", {"start": v(-5.74, 11.54) * mm, "end": v(-5.67, 11.1) * mm});
            skLineSegment(sketch, "E284", {"start": v(-5.67, 11.1) * mm, "end": v(-5.59, 10.84) * mm});
            skLineSegment(sketch, "E285", {"start": v(-5.59, 10.84) * mm, "end": v(-4.59, 8.88) * mm});
            skLineSegment(sketch, "E286", {"start": v(-4.59, 8.88) * mm, "end": v(-4.55, 8.69) * mm});
            skLineSegment(sketch, "E287", {"start": v(-4.55, 8.69) * mm, "end": v(-4.6, 8.5) * mm});
            skLineSegment(sketch, "E288", {"start": v(-4.6, 8.5) * mm, "end": v(-4.76, 8.36) * mm});
            skLineSegment(sketch, "E289", {"start": v(-4.76, 8.36) * mm, "end": v(-6.48, 7.1) * mm});
            skLineSegment(sketch, "E290", {"start": v(-6.48, 7.1) * mm, "end": v(-6.65, 7) * mm});
            skLineSegment(sketch, "E291", {"start": v(-6.65, 7) * mm, "end": v(-6.86, 7) * mm});
            skLineSegment(sketch, "E292", {"start": v(-6.86, 7) * mm, "end": v(-7.03, 7.11) * mm});
            skLineSegment(sketch, "E293", {"start": v(-7.03, 7.11) * mm, "end": v(-8.58, 8.66) * mm});
            skLineSegment(sketch, "E294", {"start": v(-8.58, 8.66) * mm, "end": v(-8.8, 8.82) * mm});
            skLineSegment(sketch, "E295", {"start": v(-8.8, 8.82) * mm, "end": v(-9.2, 9.03) * mm});
            skLineSegment(sketch, "E296", {"start": v(-9.2, 9.03) * mm, "end": v(-9.8, 9.25) * mm});
            skLineSegment(sketch, "E297", {"start": v(-9.8, 9.25) * mm, "end": v(-10.58, 9.44) * mm});
            skLineSegment(sketch, "E298", {"start": v(-10.58, 9.44) * mm, "end": v(-11.56, 9.56) * mm});
            skLineSegment(sketch, "E299", {"start": v(-11.56, 9.56) * mm, "end": v(-12.66, 8.04) * mm});
            skLineSegment(sketch, "E300", {"start": v(-12.66, 8.04) * mm, "end": v(-12.25, 7.15) * mm});
            skLineSegment(sketch, "E301", {"start": v(-12.25, 7.15) * mm, "end": v(-11.82, 6.46) * mm});
            skLineSegment(sketch, "E302", {"start": v(-11.82, 6.46) * mm, "end": v(-11.43, 5.96) * mm});
            skLineSegment(sketch, "E303", {"start": v(-11.43, 5.96) * mm, "end": v(-11.1, 5.65) * mm});
            skLineSegment(sketch, "E304", {"start": v(-11.1, 5.65) * mm, "end": v(-10.9, 5.48) * mm});
            skLineSegment(sketch, "E305", {"start": v(-10.9, 5.48) * mm, "end": v(-8.94, 4.5) * mm});
            skLineSegment(sketch, "E306", {"start": v(-8.94, 4.5) * mm, "end": v(-8.78, 4.36) * mm});
            skLineSegment(sketch, "E307", {"start": v(-8.78, 4.36) * mm, "end": v(-8.72, 4.16) * mm});
            skLineSegment(sketch, "E308", {"start": v(-8.72, 4.16) * mm, "end": v(-8.76, 3.96) * mm});
            skLineSegment(sketch, "E309", {"start": v(-8.76, 3.96) * mm, "end": v(-9.42, 1.94) * mm});
            skLineSegment(sketch, "E310", {"start": v(-9.42, 1.94) * mm, "end": v(-9.5, 1.76) * mm});
            skLineSegment(sketch, "E311", {"start": v(-9.5, 1.76) * mm, "end": v(-9.67, 1.64) * mm});
            skLineSegment(sketch, "E312", {"start": v(-9.67, 1.64) * mm, "end": v(-9.87, 1.62) * mm});
            skLineSegment(sketch, "E313", {"start": v(-9.87, 1.62) * mm, "end": v(-12.03, 1.97) * mm});
            skLineSegment(sketch, "E314", {"start": v(-12.03, 1.97) * mm, "end": v(-12.3, 1.96) * mm});
            skLineSegment(sketch, "E315", {"start": v(-12.3, 1.96) * mm, "end": v(-12.75, 1.9) * mm});
            skLineSegment(sketch, "E316", {"start": v(-12.75, 1.9) * mm, "end": v(-13.36, 1.73) * mm});
            skLineSegment(sketch, "E317", {"start": v(-13.36, 1.73) * mm, "end": v(-14.11, 1.42) * mm});
            skLineSegment(sketch, "E318", {"start": v(-14.11, 1.42) * mm, "end": v(-14.97, 0.94) * mm});
            skLineSegment(sketch, "E319", {"start": v(-14.97, 0.94) * mm, "end": v(-14.97, -0.94) * mm});
            skLineSegment(sketch, "E320", {"start": v(-14.97, -0.94) * mm, "end": v(-14.11, -1.42) * mm});
            skLineSegment(sketch, "E321", {"start": v(-14.11, -1.42) * mm, "end": v(-13.36, -1.73) * mm});
            skLineSegment(sketch, "E322", {"start": v(-13.36, -1.73) * mm, "end": v(-12.75, -1.9) * mm});
            skLineSegment(sketch, "E323", {"start": v(-12.75, -1.9) * mm, "end": v(-12.3, -1.96) * mm});
            skLineSegment(sketch, "E324", {"start": v(-12.3, -1.96) * mm, "end": v(-12.03, -1.97) * mm});
            skLineSegment(sketch, "E325", {"start": v(-12.03, -1.97) * mm, "end": v(-9.87, -1.62) * mm});
            skLineSegment(sketch, "E326", {"start": v(-9.87, -1.62) * mm, "end": v(-9.67, -1.64) * mm});
            skLineSegment(sketch, "E327", {"start": v(-9.67, -1.64) * mm, "end": v(-9.5, -1.76) * mm});
            skLineSegment(sketch, "E328", {"start": v(-9.5, -1.76) * mm, "end": v(-9.42, -1.94) * mm});
            skLineSegment(sketch, "E329", {"start": v(-9.42, -1.94) * mm, "end": v(-8.76, -3.96) * mm});
            skLineSegment(sketch, "E330", {"start": v(-8.76, -3.96) * mm, "end": v(-8.72, -4.16) * mm});
            skLineSegment(sketch, "E331", {"start": v(-8.72, -4.16) * mm, "end": v(-8.78, -4.36) * mm});
            skLineSegment(sketch, "E332", {"start": v(-8.78, -4.36) * mm, "end": v(-8.94, -4.5) * mm});
            skLineSegment(sketch, "E333", {"start": v(-8.94, -4.5) * mm, "end": v(-10.9, -5.48) * mm});
            skLineSegment(sketch, "E334", {"start": v(-10.9, -5.48) * mm, "end": v(-11.1, -5.65) * mm});
            skLineSegment(sketch, "E335", {"start": v(-11.1, -5.65) * mm, "end": v(-11.43, -5.96) * mm});
            skLineSegment(sketch, "E336", {"start": v(-11.43, -5.96) * mm, "end": v(-11.82, -6.46) * mm});
            skLineSegment(sketch, "E337", {"start": v(-11.82, -6.46) * mm, "end": v(-12.25, -7.15) * mm});
            skLineSegment(sketch, "E338", {"start": v(-12.25, -7.15) * mm, "end": v(-12.66, -8.04) * mm});
            skLineSegment(sketch, "E339", {"start": v(-12.66, -8.04) * mm, "end": v(-11.56, -9.56) * mm});
            skLineSegment(sketch, "E340", {"start": v(-11.56, -9.56) * mm, "end": v(-10.58, -9.44) * mm});
            skLineSegment(sketch, "E341", {"start": v(-10.58, -9.44) * mm, "end": v(-9.8, -9.25) * mm});
            skLineSegment(sketch, "E342", {"start": v(-9.8, -9.25) * mm, "end": v(-9.2, -9.03) * mm});
            skLineSegment(sketch, "E343", {"start": v(-9.2, -9.03) * mm, "end": v(-8.8, -8.82) * mm});
            skLineSegment(sketch, "E344", {"start": v(-8.8, -8.82) * mm, "end": v(-8.58, -8.66) * mm});
            skLineSegment(sketch, "E345", {"start": v(-8.58, -8.66) * mm, "end": v(-7.03, -7.11) * mm});
            skLineSegment(sketch, "E346", {"start": v(-7.03, -7.11) * mm, "end": v(-6.86, -7) * mm});
            skLineSegment(sketch, "E347", {"start": v(-6.86, -7) * mm, "end": v(-6.65, -7) * mm});
            skLineSegment(sketch, "E348", {"start": v(-6.65, -7) * mm, "end": v(-6.48, -7.1) * mm});
            skLineSegment(sketch, "E349", {"start": v(-6.48, -7.1) * mm, "end": v(-4.76, -8.36) * mm});
            skLineSegment(sketch, "E350", {"start": v(-4.76, -8.36) * mm, "end": v(-4.6, -8.5) * mm});
            skLineSegment(sketch, "E351", {"start": v(-4.6, -8.5) * mm, "end": v(-4.55, -8.69) * mm});
            skLineSegment(sketch, "E352", {"start": v(-4.55, -8.69) * mm, "end": v(-4.59, -8.88) * mm});
            skLineSegment(sketch, "E353", {"start": v(-4.59, -8.88) * mm, "end": v(-5.59, -10.84) * mm});
            skLineSegment(sketch, "E354", {"start": v(-5.59, -10.84) * mm, "end": v(-5.67, -11.1) * mm});
            skLineSegment(sketch, "E355", {"start": v(-5.67, -11.1) * mm, "end": v(-5.74, -11.54) * mm});
            skLineSegment(sketch, "E356", {"start": v(-5.74, -11.54) * mm, "end": v(-5.77, -12.17) * mm});
            skLineSegment(sketch, "E357", {"start": v(-5.77, -12.17) * mm, "end": v(-5.7, -12.98) * mm});
            skLineSegment(sketch, "E358", {"start": v(-5.7, -12.98) * mm, "end": v(-5.52, -13.95) * mm});
            skLineSegment(sketch, "E359", {"start": v(-5.52, -13.95) * mm, "end": v(-3.74, -14.53) * mm});
            skLineSegment(sketch, "E360", {"start": v(-3.74, -14.53) * mm, "end": v(-3.01, -13.86) * mm});
            skLineSegment(sketch, "E361", {"start": v(-3.01, -13.86) * mm, "end": v(-2.49, -13.24) * mm});
            skLineSegment(sketch, "E362", {"start": v(-2.49, -13.24) * mm, "end": v(-2.14, -12.71) * mm});
            skLineSegment(sketch, "E363", {"start": v(-2.14, -12.71) * mm, "end": v(-1.94, -12.3) * mm});
            skLineSegment(sketch, "E364", {"start": v(-1.94, -12.3) * mm, "end": v(-1.85, -12.05) * mm});
            skLineSegment(sketch, "E365", {"start": v(-1.85, -12.05) * mm, "end": v(-1.5, -9.89) * mm});
            skLineSegment(sketch, "E366", {"start": v(-1.5, -9.89) * mm, "end": v(-1.43, -9.7) * mm});
            skLineSegment(sketch, "E367", {"start": v(-1.43, -9.7) * mm, "end": v(-1.26, -9.58) * mm});
            skLineSegment(sketch, "E368", {"start": v(-1.26, -9.58) * mm, "end": v(-1.06, -9.56) * mm});
            skLineSegment(sketch, "E369", {"start": v(-1.06, -9.56) * mm, "end": v(1.06, -9.56) * mm});
            skLineSegment(sketch, "E370", {"start": v(1.06, -9.56) * mm, "end": v(1.26, -9.58) * mm});
            skLineSegment(sketch, "E371", {"start": v(1.26, -9.58) * mm, "end": v(1.43, -9.7) * mm});
            skLineSegment(sketch, "E372", {"start": v(1.43, -9.7) * mm, "end": v(1.5, -9.89) * mm});
            skLineSegment(sketch, "E373", {"start": v(1.5, -9.89) * mm, "end": v(1.85, -12.05) * mm});
            skLineSegment(sketch, "E374", {"start": v(1.85, -12.05) * mm, "end": v(1.94, -12.3) * mm});
            skLineSegment(sketch, "E375", {"start": v(1.94, -12.3) * mm, "end": v(2.14, -12.71) * mm});
            skLineSegment(sketch, "E376", {"start": v(2.14, -12.71) * mm, "end": v(2.49, -13.24) * mm});
            skLineSegment(sketch, "E377", {"start": v(2.49, -13.24) * mm, "end": v(3.01, -13.86) * mm});
            skLineSegment(sketch, "E378", {"start": v(3.01, -13.86) * mm, "end": v(3.74, -14.53) * mm});
            skLineSegment(sketch, "E379", {"start": v(3.74, -14.53) * mm, "end": v(5.52, -13.95) * mm});
            skLineSegment(sketch, "E380", {"start": v(5.52, -13.95) * mm, "end": v(5.7, -12.98) * mm});
            skLineSegment(sketch, "E381", {"start": v(5.7, -12.98) * mm, "end": v(5.77, -12.17) * mm});
            skLineSegment(sketch, "E382", {"start": v(5.77, -12.17) * mm, "end": v(5.74, -11.54) * mm});
            skLineSegment(sketch, "E383", {"start": v(5.74, -11.54) * mm, "end": v(5.67, -11.1) * mm});
            skLineSegment(sketch, "E384", {"start": v(5.67, -11.1) * mm, "end": v(5.59, -10.84) * mm});
            skLineSegment(sketch, "E385", {"start": v(5.59, -10.84) * mm, "end": v(4.59, -8.88) * mm});
            skLineSegment(sketch, "E386", {"start": v(4.59, -8.88) * mm, "end": v(4.55, -8.69) * mm});
            skLineSegment(sketch, "E387", {"start": v(4.55, -8.69) * mm, "end": v(4.6, -8.5) * mm});
            skLineSegment(sketch, "E388", {"start": v(4.6, -8.5) * mm, "end": v(4.76, -8.36) * mm});
            skLineSegment(sketch, "E389", {"start": v(4.76, -8.36) * mm, "end": v(6.48, -7.1) * mm});
            skLineSegment(sketch, "E390", {"start": v(6.48, -7.1) * mm, "end": v(6.65, -7) * mm});
            skLineSegment(sketch, "E391", {"start": v(6.65, -7) * mm, "end": v(6.86, -7) * mm});
            skLineSegment(sketch, "E392", {"start": v(6.86, -7) * mm, "end": v(7.03, -7.11) * mm});
            skLineSegment(sketch, "E393", {"start": v(7.03, -7.11) * mm, "end": v(8.58, -8.66) * mm});
            skLineSegment(sketch, "E394", {"start": v(8.58, -8.66) * mm, "end": v(8.8, -8.82) * mm});
            skLineSegment(sketch, "E395", {"start": v(8.8, -8.82) * mm, "end": v(9.2, -9.03) * mm});
            skLineSegment(sketch, "E396", {"start": v(9.2, -9.03) * mm, "end": v(9.8, -9.25) * mm});
            skLineSegment(sketch, "E397", {"start": v(9.8, -9.25) * mm, "end": v(10.58, -9.44) * mm});
            skLineSegment(sketch, "E398", {"start": v(10.58, -9.44) * mm, "end": v(11.56, -9.56) * mm});
            skLineSegment(sketch, "E399", {"start": v(11.56, -9.56) * mm, "end": v(12.66, -8.04) * mm});
            skLineSegment(sketch, "E400", {"start": v(2.5, 0) * mm, "end": v(2.48, 0.33) * mm});
            skLineSegment(sketch, "E401", {"start": v(2.48, 0.33) * mm, "end": v(2.41, 0.65) * mm});
            skLineSegment(sketch, "E402", {"start": v(2.41, 0.65) * mm, "end": v(2.3, 0.96) * mm});
            skLineSegment(sketch, "E403", {"start": v(2.3, 0.96) * mm, "end": v(2.17, 1.25) * mm});
            skLineSegment(sketch, "E404", {"start": v(2.17, 1.25) * mm, "end": v(1.98, 1.52) * mm});
            skLineSegment(sketch, "E405", {"start": v(1.98, 1.52) * mm, "end": v(1.77, 1.77) * mm});
            skLineSegment(sketch, "E406", {"start": v(1.77, 1.77) * mm, "end": v(1.52, 1.98) * mm});
            skLineSegment(sketch, "E407", {"start": v(1.52, 1.98) * mm, "end": v(1.25, 2.17) * mm});
            skLineSegment(sketch, "E408", {"start": v(1.25, 2.17) * mm, "end": v(0.96, 2.3) * mm});
            skLineSegment(sketch, "E409", {"start": v(0.96, 2.3) * mm, "end": v(0.65, 2.41) * mm});
            skLineSegment(sketch, "E410", {"start": v(0.65, 2.41) * mm, "end": v(0.33, 2.48) * mm});
            skLineSegment(sketch, "E411", {"start": v(0.33, 2.48) * mm, "end": v(0, 2.5) * mm});
            skLineSegment(sketch, "E412", {"start": v(0, 2.5) * mm, "end": v(-0.33, 2.48) * mm});
            skLineSegment(sketch, "E413", {"start": v(-0.33, 2.48) * mm, "end": v(-0.65, 2.41) * mm});
            skLineSegment(sketch, "E414", {"start": v(-0.65, 2.41) * mm, "end": v(-0.96, 2.3) * mm});
            skLineSegment(sketch, "E415", {"start": v(-0.96, 2.3) * mm, "end": v(-1.25, 2.17) * mm});
            skLineSegment(sketch, "E416", {"start": v(-1.25, 2.17) * mm, "end": v(-1.52, 1.98) * mm});
            skLineSegment(sketch, "E417", {"start": v(-1.52, 1.98) * mm, "end": v(-1.77, 1.77) * mm});
            skLineSegment(sketch, "E418", {"start": v(-1.77, 1.77) * mm, "end": v(-1.98, 1.52) * mm});
            skLineSegment(sketch, "E419", {"start": v(-1.98, 1.52) * mm, "end": v(-2.17, 1.25) * mm});
            skLineSegment(sketch, "E420", {"start": v(-2.17, 1.25) * mm, "end": v(-2.3, 0.96) * mm});
            skLineSegment(sketch, "E421", {"start": v(-2.3, 0.96) * mm, "end": v(-2.41, 0.65) * mm});
            skLineSegment(sketch, "E422", {"start": v(-2.41, 0.65) * mm, "end": v(-2.48, 0.33) * mm});
            skLineSegment(sketch, "E423", {"start": v(-2.48, 0.33) * mm, "end": v(-2.5, 0) * mm});
            skLineSegment(sketch, "E424", {"start": v(-2.5, 0) * mm, "end": v(-2.48, -0.33) * mm});
            skLineSegment(sketch, "E425", {"start": v(-2.48, -0.33) * mm, "end": v(-2.41, -0.65) * mm});
            skLineSegment(sketch, "E426", {"start": v(-2.41, -0.65) * mm, "end": v(-2.3, -0.96) * mm});
            skLineSegment(sketch, "E427", {"start": v(-2.3, -0.96) * mm, "end": v(-2.17, -1.25) * mm});
            skLineSegment(sketch, "E428", {"start": v(-2.17, -1.25) * mm, "end": v(-1.98, -1.52) * mm});
            skLineSegment(sketch, "E429", {"start": v(-1.98, -1.52) * mm, "end": v(-1.77, -1.77) * mm});
            skLineSegment(sketch, "E430", {"start": v(-1.77, -1.77) * mm, "end": v(-1.52, -1.98) * mm});
            skLineSegment(sketch, "E431", {"start": v(-1.52, -1.98) * mm, "end": v(-1.25, -2.17) * mm});
            skLineSegment(sketch, "E432", {"start": v(-1.25, -2.17) * mm, "end": v(-0.96, -2.3) * mm});
            skLineSegment(sketch, "E433", {"start": v(-0.96, -2.3) * mm, "end": v(-0.65, -2.41) * mm});
            skLineSegment(sketch, "E434", {"start": v(-0.65, -2.41) * mm, "end": v(-0.33, -2.48) * mm});
            skLineSegment(sketch, "E435", {"start": v(-0.33, -2.48) * mm, "end": v(0, -2.5) * mm});
            skLineSegment(sketch, "E436", {"start": v(0, -2.5) * mm, "end": v(0.33, -2.48) * mm});
            skLineSegment(sketch, "E437", {"start": v(0.33, -2.48) * mm, "end": v(0.65, -2.41) * mm});
            skLineSegment(sketch, "E438", {"start": v(0.65, -2.41) * mm, "end": v(0.96, -2.3) * mm});
            skLineSegment(sketch, "E439", {"start": v(0.96, -2.3) * mm, "end": v(1.25, -2.17) * mm});
            skLineSegment(sketch, "E440", {"start": v(1.25, -2.17) * mm, "end": v(1.52, -1.98) * mm});
            skLineSegment(sketch, "E441", {"start": v(1.52, -1.98) * mm, "end": v(1.77, -1.77) * mm});
            skLineSegment(sketch, "E442", {"start": v(1.77, -1.77) * mm, "end": v(1.98, -1.52) * mm});
            skLineSegment(sketch, "E443", {"start": v(1.98, -1.52) * mm, "end": v(2.17, -1.25) * mm});
            skLineSegment(sketch, "E444", {"start": v(2.17, -1.25) * mm, "end": v(2.3, -0.96) * mm});
            skLineSegment(sketch, "E445", {"start": v(2.3, -0.96) * mm, "end": v(2.41, -0.65) * mm});
            skLineSegment(sketch, "E446", {"start": v(2.41, -0.65) * mm, "end": v(2.48, -0.33) * mm});
            skLineSegment(sketch, "E447", {"start": v(2.48, -0.33) * mm, "end": v(2.5, 0) * mm});
            skSolve(sketch);
        }
        {
            var Q0;
            Q0 = qSketchRegion(id + "F2", true);
            extrude(context, id + "F3", {"entities" : qUnion([Q0]), "depth" : 4 * mm});
        }
        {
            var Q0;
            Q0=qCreatedBy(makeId("Front.planeOp"),FACE);
            var sketch = newSketch(context, id + "F4", { "sketchPlane" : qUnion([Q0])});
            skLineSegment(sketch, "E448", {"start": v(13.97, -7.96) * mm, "end": v(13.6, -7.28) * mm});
            skLineSegment(sketch, "E449", {"start": v(13.6, -7.28) * mm, "end": v(13.1, -6.54) * mm});
            skLineSegment(sketch, "E450", {"start": v(13.1, -6.54) * mm, "end": v(12.65, -6.01) * mm});
            skLineSegment(sketch, "E451", {"start": v(12.65, -6.01) * mm, "end": v(12.28, -5.68) * mm});
            skLineSegment(sketch, "E452", {"start": v(12.28, -5.68) * mm, "end": v(12.03, -5.51) * mm});
            skLineSegment(sketch, "E453", {"start": v(12.03, -5.51) * mm, "end": v(10.07, -4.62) * mm});
            skLineSegment(sketch, "E454", {"start": v(10.07, -4.62) * mm, "end": v(9.9, -4.49) * mm});
            skLineSegment(sketch, "E455", {"start": v(9.9, -4.49) * mm, "end": v(9.84, -4.3) * mm});
            skLineSegment(sketch, "E456", {"start": v(9.84, -4.3) * mm, "end": v(9.87, -4.1) * mm});
            skLineSegment(sketch, "E457", {"start": v(9.87, -4.1) * mm, "end": v(10.49, -2) * mm});
            skLineSegment(sketch, "E458", {"start": v(10.49, -2) * mm, "end": v(10.57, -1.8) * mm});
            skLineSegment(sketch, "E459", {"start": v(10.57, -1.8) * mm, "end": v(10.73, -1.69) * mm});
            skLineSegment(sketch, "E460", {"start": v(10.73, -1.69) * mm, "end": v(10.93, -1.66) * mm});
            skLineSegment(sketch, "E461", {"start": v(10.93, -1.66) * mm, "end": v(13.07, -1.97) * mm});
            skLineSegment(sketch, "E462", {"start": v(13.07, -1.97) * mm, "end": v(13.37, -1.96) * mm});
            skLineSegment(sketch, "E463", {"start": v(13.37, -1.96) * mm, "end": v(13.86, -1.88) * mm});
            skLineSegment(sketch, "E464", {"start": v(13.86, -1.88) * mm, "end": v(14.53, -1.69) * mm});
            skLineSegment(sketch, "E465", {"start": v(14.53, -1.69) * mm, "end": v(15.35, -1.34) * mm});
            skLineSegment(sketch, "E466", {"start": v(15.35, -1.34) * mm, "end": v(16.03, -0.96) * mm});
            skLineSegment(sketch, "E467", {"start": v(16.03, -0.96) * mm, "end": v(16.03, 0.96) * mm});
            skLineSegment(sketch, "E468", {"start": v(16.03, 0.96) * mm, "end": v(15.35, 1.34) * mm});
            skLineSegment(sketch, "E469", {"start": v(15.35, 1.34) * mm, "end": v(14.53, 1.69) * mm});
            skLineSegment(sketch, "E470", {"start": v(14.53, 1.69) * mm, "end": v(13.86, 1.88) * mm});
            skLineSegment(sketch, "E471", {"start": v(13.86, 1.88) * mm, "end": v(13.37, 1.96) * mm});
            skLineSegment(sketch, "E472", {"start": v(13.37, 1.96) * mm, "end": v(13.07, 1.97) * mm});
            skLineSegment(sketch, "E473", {"start": v(13.07, 1.97) * mm, "end": v(10.93, 1.66) * mm});
            skLineSegment(sketch, "E474", {"start": v(10.93, 1.66) * mm, "end": v(10.73, 1.69) * mm});
            skLineSegment(sketch, "E475", {"start": v(10.73, 1.69) * mm, "end": v(10.57, 1.8) * mm});
            skLineSegment(sketch, "E476", {"start": v(10.57, 1.8) * mm, "end": v(10.49, 2) * mm});
            skLineSegment(sketch, "E477", {"start": v(10.49, 2) * mm, "end": v(9.87, 4.1) * mm});
            skLineSegment(sketch, "E478", {"start": v(9.87, 4.1) * mm, "end": v(9.84, 4.3) * mm});
            skLineSegment(sketch, "E479", {"start": v(9.84, 4.3) * mm, "end": v(9.9, 4.49) * mm});
            skLineSegment(sketch, "E480", {"start": v(9.9, 4.49) * mm, "end": v(10.07, 4.62) * mm});
            skLineSegment(sketch, "E481", {"start": v(10.07, 4.62) * mm, "end": v(12.03, 5.51) * mm});
            skLineSegment(sketch, "E482", {"start": v(12.03, 5.51) * mm, "end": v(12.28, 5.68) * mm});
            skLineSegment(sketch, "E483", {"start": v(12.28, 5.68) * mm, "end": v(12.65, 6.01) * mm});
            skLineSegment(sketch, "E484", {"start": v(12.65, 6.01) * mm, "end": v(13.1, 6.54) * mm});
            skLineSegment(sketch, "E485", {"start": v(13.1, 6.54) * mm, "end": v(13.6, 7.28) * mm});
            skLineSegment(sketch, "E486", {"start": v(13.6, 7.28) * mm, "end": v(13.97, 7.96) * mm});
            skLineSegment(sketch, "E487", {"start": v(13.97, 7.96) * mm, "end": v(12.93, 9.58) * mm});
            skLineSegment(sketch, "E488", {"start": v(12.93, 9.58) * mm, "end": v(12.16, 9.53) * mm});
            skLineSegment(sketch, "E489", {"start": v(12.16, 9.53) * mm, "end": v(11.28, 9.38) * mm});
            skLineSegment(sketch, "E490", {"start": v(11.28, 9.38) * mm, "end": v(10.61, 9.18) * mm});
            skLineSegment(sketch, "E491", {"start": v(10.61, 9.18) * mm, "end": v(10.16, 8.98) * mm});
            skLineSegment(sketch, "E492", {"start": v(10.16, 8.98) * mm, "end": v(9.9, 8.83) * mm});
            skLineSegment(sketch, "E493", {"start": v(9.9, 8.83) * mm, "end": v(8.27, 7.41) * mm});
            skLineSegment(sketch, "E494", {"start": v(8.27, 7.41) * mm, "end": v(8.09, 7.32) * mm});
            skLineSegment(sketch, "E495", {"start": v(8.09, 7.32) * mm, "end": v(7.88, 7.34) * mm});
            skLineSegment(sketch, "E496", {"start": v(7.88, 7.34) * mm, "end": v(7.71, 7.45) * mm});
            skLineSegment(sketch, "E497", {"start": v(7.71, 7.45) * mm, "end": v(6.06, 8.89) * mm});
            skLineSegment(sketch, "E498", {"start": v(6.06, 8.89) * mm, "end": v(5.92, 9.04) * mm});
            skLineSegment(sketch, "E499", {"start": v(5.92, 9.04) * mm, "end": v(5.88, 9.24) * mm});
            skLineSegment(sketch, "E500", {"start": v(5.88, 9.24) * mm, "end": v(5.94, 9.43) * mm});
            skLineSegment(sketch, "E501", {"start": v(5.94, 9.43) * mm, "end": v(7.11, 11.25) * mm});
            skLineSegment(sketch, "E502", {"start": v(7.11, 11.25) * mm, "end": v(7.23, 11.52) * mm});
            skLineSegment(sketch, "E503", {"start": v(7.23, 11.52) * mm, "end": v(7.36, 12) * mm});
            skLineSegment(sketch, "E504", {"start": v(7.36, 12) * mm, "end": v(7.46, 12.69) * mm});
            skLineSegment(sketch, "E505", {"start": v(7.46, 12.69) * mm, "end": v(7.48, 13.58) * mm});
            skLineSegment(sketch, "E506", {"start": v(7.48, 13.58) * mm, "end": v(7.42, 14.36) * mm});
            skLineSegment(sketch, "E507", {"start": v(7.42, 14.36) * mm, "end": v(5.67, 15.15) * mm});
            skLineSegment(sketch, "E508", {"start": v(5.67, 15.15) * mm, "end": v(5.05, 14.7) * mm});
            skLineSegment(sketch, "E509", {"start": v(5.05, 14.7) * mm, "end": v(4.39, 14.1) * mm});
            skLineSegment(sketch, "E510", {"start": v(4.39, 14.1) * mm, "end": v(3.93, 13.56) * mm});
            skLineSegment(sketch, "E511", {"start": v(3.93, 13.56) * mm, "end": v(3.66, 13.15) * mm});
            skLineSegment(sketch, "E512", {"start": v(3.66, 13.15) * mm, "end": v(3.52, 12.89) * mm});
            skLineSegment(sketch, "E513", {"start": v(3.52, 12.89) * mm, "end": v(2.92, 10.81) * mm});
            skLineSegment(sketch, "E514", {"start": v(2.92, 10.81) * mm, "end": v(2.81, 10.64) * mm});
            skLineSegment(sketch, "E515", {"start": v(2.81, 10.64) * mm, "end": v(2.63, 10.54) * mm});
            skLineSegment(sketch, "E516", {"start": v(2.63, 10.54) * mm, "end": v(2.43, 10.54) * mm});
            skLineSegment(sketch, "E517", {"start": v(2.43, 10.54) * mm, "end": v(0.26, 10.86) * mm});
            skLineSegment(sketch, "E518", {"start": v(0.26, 10.86) * mm, "end": v(0.06, 10.9) * mm});
            skLineSegment(sketch, "E519", {"start": v(0.06, 10.9) * mm, "end": v(-0.08, 11.05) * mm});
            skLineSegment(sketch, "E520", {"start": v(-0.08, 11.05) * mm, "end": v(-0.13, 11.25) * mm});
            skLineSegment(sketch, "E521", {"start": v(-0.13, 11.25) * mm, "end": v(-0.13, 13.41) * mm});
            skLineSegment(sketch, "E522", {"start": v(-0.13, 13.41) * mm, "end": v(-0.18, 13.7) * mm});
            skLineSegment(sketch, "E523", {"start": v(-0.18, 13.7) * mm, "end": v(-0.33, 14.18) * mm});
            skLineSegment(sketch, "E524", {"start": v(-0.33, 14.18) * mm, "end": v(-0.62, 14.81) * mm});
            skLineSegment(sketch, "E525", {"start": v(-0.62, 14.81) * mm, "end": v(-1.08, 15.57) * mm});
            skLineSegment(sketch, "E526", {"start": v(-1.08, 15.57) * mm, "end": v(-1.55, 16.2) * mm});
            skLineSegment(sketch, "E527", {"start": v(-1.55, 16.2) * mm, "end": v(-3.45, 15.92) * mm});
            skLineSegment(sketch, "E528", {"start": v(-3.45, 15.92) * mm, "end": v(-3.73, 15.2) * mm});
            skLineSegment(sketch, "E529", {"start": v(-3.73, 15.2) * mm, "end": v(-3.96, 14.33) * mm});
            skLineSegment(sketch, "E530", {"start": v(-3.96, 14.33) * mm, "end": v(-4.06, 13.64) * mm});
            skLineSegment(sketch, "E531", {"start": v(-4.06, 13.64) * mm, "end": v(-4.07, 13.15) * mm});
            skLineSegment(sketch, "E532", {"start": v(-4.07, 13.15) * mm, "end": v(-4.04, 12.85) * mm});
            skLineSegment(sketch, "E533", {"start": v(-4.04, 12.85) * mm, "end": v(-3.42, 10.78) * mm});
            skLineSegment(sketch, "E534", {"start": v(-3.42, 10.78) * mm, "end": v(-3.42, 10.57) * mm});
            skLineSegment(sketch, "E535", {"start": v(-3.42, 10.57) * mm, "end": v(-3.51, 10.4) * mm});
            skLineSegment(sketch, "E536", {"start": v(-3.51, 10.4) * mm, "end": v(-3.69, 10.29) * mm});
            skLineSegment(sketch, "E537", {"start": v(-3.69, 10.29) * mm, "end": v(-5.68, 9.38) * mm});
            skLineSegment(sketch, "E538", {"start": v(-5.68, 9.38) * mm, "end": v(-5.88, 9.32) * mm});
            skLineSegment(sketch, "E539", {"start": v(-5.88, 9.32) * mm, "end": v(-6.07, 9.36) * mm});
            skLineSegment(sketch, "E540", {"start": v(-6.07, 9.36) * mm, "end": v(-6.22, 9.5) * mm});
            skLineSegment(sketch, "E541", {"start": v(-6.22, 9.5) * mm, "end": v(-7.39, 11.32) * mm});
            skLineSegment(sketch, "E542", {"start": v(-7.39, 11.32) * mm, "end": v(-7.6, 11.53) * mm});
            skLineSegment(sketch, "E543", {"start": v(-7.6, 11.53) * mm, "end": v(-7.97, 11.85) * mm});
            skLineSegment(sketch, "E544", {"start": v(-7.97, 11.85) * mm, "end": v(-8.56, 12.23) * mm});
            skLineSegment(sketch, "E545", {"start": v(-8.56, 12.23) * mm, "end": v(-9.36, 12.62) * mm});
            skLineSegment(sketch, "E546", {"start": v(-9.36, 12.62) * mm, "end": v(-10.1, 12.89) * mm});
            skLineSegment(sketch, "E547", {"start": v(-10.1, 12.89) * mm, "end": v(-11.54, 11.63) * mm});
            skLineSegment(sketch, "E548", {"start": v(-11.54, 11.63) * mm, "end": v(-11.38, 10.87) * mm});
            skLineSegment(sketch, "E549", {"start": v(-11.38, 10.87) * mm, "end": v(-11.1, 10.02) * mm});
            skLineSegment(sketch, "E550", {"start": v(-11.1, 10.02) * mm, "end": v(-10.82, 9.39) * mm});
            skLineSegment(sketch, "E551", {"start": v(-10.82, 9.39) * mm, "end": v(-10.56, 8.97) * mm});
            skLineSegment(sketch, "E552", {"start": v(-10.56, 8.97) * mm, "end": v(-10.37, 8.73) * mm});
            skLineSegment(sketch, "E553", {"start": v(-10.37, 8.73) * mm, "end": v(-8.74, 7.32) * mm});
            skLineSegment(sketch, "E554", {"start": v(-8.74, 7.32) * mm, "end": v(-8.62, 7.15) * mm});
            skLineSegment(sketch, "E555", {"start": v(-8.62, 7.15) * mm, "end": v(-8.6, 6.95) * mm});
            skLineSegment(sketch, "E556", {"start": v(-8.6, 6.95) * mm, "end": v(-8.7, 6.77) * mm});
            skLineSegment(sketch, "E557", {"start": v(-8.7, 6.77) * mm, "end": v(-9.88, 4.92) * mm});
            skLineSegment(sketch, "E558", {"start": v(-9.88, 4.92) * mm, "end": v(-10, 4.77) * mm});
            skLineSegment(sketch, "E559", {"start": v(-10, 4.77) * mm, "end": v(-10.2, 4.7) * mm});
            skLineSegment(sketch, "E560", {"start": v(-10.2, 4.7) * mm, "end": v(-10.4, 4.73) * mm});
            skLineSegment(sketch, "E561", {"start": v(-10.4, 4.73) * mm, "end": v(-12.36, 5.63) * mm});
            skLineSegment(sketch, "E562", {"start": v(-12.36, 5.63) * mm, "end": v(-12.65, 5.7) * mm});
            skLineSegment(sketch, "E563", {"start": v(-12.65, 5.7) * mm, "end": v(-13.15, 5.76) * mm});
            skLineSegment(sketch, "E564", {"start": v(-13.15, 5.76) * mm, "end": v(-13.84, 5.77) * mm});
            skLineSegment(sketch, "E565", {"start": v(-13.84, 5.77) * mm, "end": v(-14.73, 5.66) * mm});
            skLineSegment(sketch, "E566", {"start": v(-14.73, 5.66) * mm, "end": v(-15.49, 5.5) * mm});
            skLineSegment(sketch, "E567", {"start": v(-15.49, 5.5) * mm, "end": v(-16.03, 3.65) * mm});
            skLineSegment(sketch, "E568", {"start": v(-16.03, 3.65) * mm, "end": v(-15.48, 3.1) * mm});
            skLineSegment(sketch, "E569", {"start": v(-15.48, 3.1) * mm, "end": v(-14.8, 2.53) * mm});
            skLineSegment(sketch, "E570", {"start": v(-14.8, 2.53) * mm, "end": v(-14.2, 2.15) * mm});
            skLineSegment(sketch, "E571", {"start": v(-14.2, 2.15) * mm, "end": v(-13.76, 1.94) * mm});
            skLineSegment(sketch, "E572", {"start": v(-13.76, 1.94) * mm, "end": v(-13.48, 1.84) * mm});
            skLineSegment(sketch, "E573", {"start": v(-13.48, 1.84) * mm, "end": v(-11.34, 1.54) * mm});
            skLineSegment(sketch, "E574", {"start": v(-11.34, 1.54) * mm, "end": v(-11.15, 1.46) * mm});
            skLineSegment(sketch, "E575", {"start": v(-11.15, 1.46) * mm, "end": v(-11.03, 1.3) * mm});
            skLineSegment(sketch, "E576", {"start": v(-11.03, 1.3) * mm, "end": v(-11, 1.1) * mm});
            skLineSegment(sketch, "E577", {"start": v(-11, 1.1) * mm, "end": v(-11, -1.1) * mm});
            skLineSegment(sketch, "E578", {"start": v(-11, -1.1) * mm, "end": v(-11.03, -1.3) * mm});
            skLineSegment(sketch, "E579", {"start": v(-11.03, -1.3) * mm, "end": v(-11.15, -1.46) * mm});
            skLineSegment(sketch, "E580", {"start": v(-11.15, -1.46) * mm, "end": v(-11.34, -1.54) * mm});
            skLineSegment(sketch, "E581", {"start": v(-11.34, -1.54) * mm, "end": v(-13.48, -1.84) * mm});
            skLineSegment(sketch, "E582", {"start": v(-13.48, -1.84) * mm, "end": v(-13.76, -1.94) * mm});
            skLineSegment(sketch, "E583", {"start": v(-13.76, -1.94) * mm, "end": v(-14.2, -2.15) * mm});
            skLineSegment(sketch, "E584", {"start": v(-14.2, -2.15) * mm, "end": v(-14.8, -2.53) * mm});
            skLineSegment(sketch, "E585", {"start": v(-14.8, -2.53) * mm, "end": v(-15.48, -3.1) * mm});
            skLineSegment(sketch, "E586", {"start": v(-15.48, -3.1) * mm, "end": v(-16.03, -3.65) * mm});
            skLineSegment(sketch, "E587", {"start": v(-16.03, -3.65) * mm, "end": v(-15.49, -5.5) * mm});
            skLineSegment(sketch, "E588", {"start": v(-15.49, -5.5) * mm, "end": v(-14.73, -5.66) * mm});
            skLineSegment(sketch, "E589", {"start": v(-14.73, -5.66) * mm, "end": v(-13.84, -5.77) * mm});
            skLineSegment(sketch, "E590", {"start": v(-13.84, -5.77) * mm, "end": v(-13.15, -5.76) * mm});
            skLineSegment(sketch, "E591", {"start": v(-13.15, -5.76) * mm, "end": v(-12.65, -5.7) * mm});
            skLineSegment(sketch, "E592", {"start": v(-12.65, -5.7) * mm, "end": v(-12.36, -5.63) * mm});
            skLineSegment(sketch, "E593", {"start": v(-12.36, -5.63) * mm, "end": v(-10.4, -4.73) * mm});
            skLineSegment(sketch, "E594", {"start": v(-10.4, -4.73) * mm, "end": v(-10.2, -4.7) * mm});
            skLineSegment(sketch, "E595", {"start": v(-10.2, -4.7) * mm, "end": v(-10, -4.77) * mm});
            skLineSegment(sketch, "E596", {"start": v(-10, -4.77) * mm, "end": v(-9.88, -4.92) * mm});
            skLineSegment(sketch, "E597", {"start": v(-9.88, -4.92) * mm, "end": v(-8.7, -6.77) * mm});
            skLineSegment(sketch, "E598", {"start": v(-8.7, -6.77) * mm, "end": v(-8.6, -6.95) * mm});
            skLineSegment(sketch, "E599", {"start": v(-8.6, -6.95) * mm, "end": v(-8.62, -7.15) * mm});
            skLineSegment(sketch, "E600", {"start": v(-8.62, -7.15) * mm, "end": v(-8.74, -7.32) * mm});
            skLineSegment(sketch, "E601", {"start": v(-8.74, -7.32) * mm, "end": v(-10.37, -8.73) * mm});
            skLineSegment(sketch, "E602", {"start": v(-10.37, -8.73) * mm, "end": v(-10.56, -8.97) * mm});
            skLineSegment(sketch, "E603", {"start": v(-10.56, -8.97) * mm, "end": v(-10.82, -9.39) * mm});
            skLineSegment(sketch, "E604", {"start": v(-10.82, -9.39) * mm, "end": v(-11.1, -10.02) * mm});
            skLineSegment(sketch, "E605", {"start": v(-11.1, -10.02) * mm, "end": v(-11.38, -10.87) * mm});
            skLineSegment(sketch, "E606", {"start": v(-11.38, -10.87) * mm, "end": v(-11.54, -11.63) * mm});
            skLineSegment(sketch, "E607", {"start": v(-11.54, -11.63) * mm, "end": v(-10.1, -12.89) * mm});
            skLineSegment(sketch, "E608", {"start": v(-10.1, -12.89) * mm, "end": v(-9.36, -12.62) * mm});
            skLineSegment(sketch, "E609", {"start": v(-9.36, -12.62) * mm, "end": v(-8.56, -12.23) * mm});
            skLineSegment(sketch, "E610", {"start": v(-8.56, -12.23) * mm, "end": v(-7.97, -11.85) * mm});
            skLineSegment(sketch, "E611", {"start": v(-7.97, -11.85) * mm, "end": v(-7.6, -11.53) * mm});
            skLineSegment(sketch, "E612", {"start": v(-7.6, -11.53) * mm, "end": v(-7.39, -11.32) * mm});
            skLineSegment(sketch, "E613", {"start": v(-7.39, -11.32) * mm, "end": v(-6.22, -9.5) * mm});
            skLineSegment(sketch, "E614", {"start": v(-6.22, -9.5) * mm, "end": v(-6.07, -9.36) * mm});
            skLineSegment(sketch, "E615", {"start": v(-6.07, -9.36) * mm, "end": v(-5.88, -9.32) * mm});
            skLineSegment(sketch, "E616", {"start": v(-5.88, -9.32) * mm, "end": v(-5.68, -9.38) * mm});
            skLineSegment(sketch, "E617", {"start": v(-5.68, -9.38) * mm, "end": v(-3.69, -10.29) * mm});
            skLineSegment(sketch, "E618", {"start": v(-3.69, -10.29) * mm, "end": v(-3.51, -10.4) * mm});
            skLineSegment(sketch, "E619", {"start": v(-3.51, -10.4) * mm, "end": v(-3.42, -10.57) * mm});
            skLineSegment(sketch, "E620", {"start": v(-3.42, -10.57) * mm, "end": v(-3.42, -10.78) * mm});
            skLineSegment(sketch, "E621", {"start": v(-3.42, -10.78) * mm, "end": v(-4.04, -12.85) * mm});
            skLineSegment(sketch, "E622", {"start": v(-4.04, -12.85) * mm, "end": v(-4.07, -13.15) * mm});
            skLineSegment(sketch, "E623", {"start": v(-4.07, -13.15) * mm, "end": v(-4.06, -13.64) * mm});
            skLineSegment(sketch, "E624", {"start": v(-4.06, -13.64) * mm, "end": v(-3.96, -14.33) * mm});
            skLineSegment(sketch, "E625", {"start": v(-3.96, -14.33) * mm, "end": v(-3.73, -15.2) * mm});
            skLineSegment(sketch, "E626", {"start": v(-3.73, -15.2) * mm, "end": v(-3.45, -15.92) * mm});
            skLineSegment(sketch, "E627", {"start": v(-3.45, -15.92) * mm, "end": v(-1.55, -16.2) * mm});
            skLineSegment(sketch, "E628", {"start": v(-1.55, -16.2) * mm, "end": v(-1.08, -15.57) * mm});
            skLineSegment(sketch, "E629", {"start": v(-1.08, -15.57) * mm, "end": v(-0.62, -14.81) * mm});
            skLineSegment(sketch, "E630", {"start": v(-0.62, -14.81) * mm, "end": v(-0.33, -14.18) * mm});
            skLineSegment(sketch, "E631", {"start": v(-0.33, -14.18) * mm, "end": v(-0.18, -13.7) * mm});
            skLineSegment(sketch, "E632", {"start": v(-0.18, -13.7) * mm, "end": v(-0.13, -13.41) * mm});
            skLineSegment(sketch, "E633", {"start": v(-0.13, -13.41) * mm, "end": v(-0.13, -11.25) * mm});
            skLineSegment(sketch, "E634", {"start": v(-0.13, -11.25) * mm, "end": v(-0.08, -11.05) * mm});
            skLineSegment(sketch, "E635", {"start": v(-0.08, -11.05) * mm, "end": v(0.06, -10.9) * mm});
            skLineSegment(sketch, "E636", {"start": v(0.06, -10.9) * mm, "end": v(0.26, -10.86) * mm});
            skLineSegment(sketch, "E637", {"start": v(0.26, -10.86) * mm, "end": v(2.43, -10.54) * mm});
            skLineSegment(sketch, "E638", {"start": v(2.43, -10.54) * mm, "end": v(2.63, -10.54) * mm});
            skLineSegment(sketch, "E639", {"start": v(2.63, -10.54) * mm, "end": v(2.81, -10.64) * mm});
            skLineSegment(sketch, "E640", {"start": v(2.81, -10.64) * mm, "end": v(2.92, -10.81) * mm});
            skLineSegment(sketch, "E641", {"start": v(2.92, -10.81) * mm, "end": v(3.52, -12.89) * mm});
            skLineSegment(sketch, "E642", {"start": v(3.52, -12.89) * mm, "end": v(3.66, -13.15) * mm});
            skLineSegment(sketch, "E643", {"start": v(3.66, -13.15) * mm, "end": v(3.93, -13.56) * mm});
            skLineSegment(sketch, "E644", {"start": v(3.93, -13.56) * mm, "end": v(4.39, -14.1) * mm});
            skLineSegment(sketch, "E645", {"start": v(4.39, -14.1) * mm, "end": v(5.05, -14.7) * mm});
            skLineSegment(sketch, "E646", {"start": v(5.05, -14.7) * mm, "end": v(5.67, -15.15) * mm});
            skLineSegment(sketch, "E647", {"start": v(5.67, -15.15) * mm, "end": v(7.42, -14.36) * mm});
            skLineSegment(sketch, "E648", {"start": v(7.42, -14.36) * mm, "end": v(7.48, -13.58) * mm});
            skLineSegment(sketch, "E649", {"start": v(7.48, -13.58) * mm, "end": v(7.46, -12.69) * mm});
            skLineSegment(sketch, "E650", {"start": v(7.46, -12.69) * mm, "end": v(7.36, -12) * mm});
            skLineSegment(sketch, "E651", {"start": v(7.36, -12) * mm, "end": v(7.23, -11.52) * mm});
            skLineSegment(sketch, "E652", {"start": v(7.23, -11.52) * mm, "end": v(7.11, -11.25) * mm});
            skLineSegment(sketch, "E653", {"start": v(7.11, -11.25) * mm, "end": v(5.94, -9.43) * mm});
            skLineSegment(sketch, "E654", {"start": v(5.94, -9.43) * mm, "end": v(5.88, -9.24) * mm});
            skLineSegment(sketch, "E655", {"start": v(5.88, -9.24) * mm, "end": v(5.92, -9.04) * mm});
            skLineSegment(sketch, "E656", {"start": v(5.92, -9.04) * mm, "end": v(6.06, -8.89) * mm});
            skLineSegment(sketch, "E657", {"start": v(6.06, -8.89) * mm, "end": v(7.71, -7.45) * mm});
            skLineSegment(sketch, "E658", {"start": v(7.71, -7.45) * mm, "end": v(7.88, -7.34) * mm});
            skLineSegment(sketch, "E659", {"start": v(7.88, -7.34) * mm, "end": v(8.09, -7.32) * mm});
            skLineSegment(sketch, "E660", {"start": v(8.09, -7.32) * mm, "end": v(8.27, -7.41) * mm});
            skLineSegment(sketch, "E661", {"start": v(8.27, -7.41) * mm, "end": v(9.9, -8.83) * mm});
            skLineSegment(sketch, "E662", {"start": v(9.9, -8.83) * mm, "end": v(10.16, -8.98) * mm});
            skLineSegment(sketch, "E663", {"start": v(10.16, -8.98) * mm, "end": v(10.61, -9.18) * mm});
            skLineSegment(sketch, "E664", {"start": v(10.61, -9.18) * mm, "end": v(11.28, -9.38) * mm});
            skLineSegment(sketch, "E665", {"start": v(11.28, -9.38) * mm, "end": v(12.16, -9.53) * mm});
            skLineSegment(sketch, "E666", {"start": v(12.16, -9.53) * mm, "end": v(12.93, -9.58) * mm});
            skLineSegment(sketch, "E667", {"start": v(12.93, -9.58) * mm, "end": v(13.97, -7.96) * mm});
            skLineSegment(sketch, "E668", {"start": v(2.3, 0) * mm, "end": v(2.29, 0.33) * mm});
            skLineSegment(sketch, "E669", {"start": v(2.29, 0.33) * mm, "end": v(2.22, 0.65) * mm});
            skLineSegment(sketch, "E670", {"start": v(2.22, 0.65) * mm, "end": v(2.12, 0.96) * mm});
            skLineSegment(sketch, "E671", {"start": v(2.12, 0.96) * mm, "end": v(1.97, 1.25) * mm});
            skLineSegment(sketch, "E672", {"start": v(1.97, 1.25) * mm, "end": v(1.79, 1.52) * mm});
            skLineSegment(sketch, "E673", {"start": v(1.79, 1.52) * mm, "end": v(1.57, 1.77) * mm});
            skLineSegment(sketch, "E674", {"start": v(1.57, 1.77) * mm, "end": v(1.33, 1.98) * mm});
            skLineSegment(sketch, "E675", {"start": v(1.33, 1.98) * mm, "end": v(1.06, 2.17) * mm});
            skLineSegment(sketch, "E676", {"start": v(1.06, 2.17) * mm, "end": v(0.76, 2.3) * mm});
            skLineSegment(sketch, "E677", {"start": v(0.76, 2.3) * mm, "end": v(0.45, 2.41) * mm});
            skLineSegment(sketch, "E678", {"start": v(0.45, 2.41) * mm, "end": v(0.13, 2.48) * mm});
            skLineSegment(sketch, "E679", {"start": v(0.13, 2.48) * mm, "end": v(-0.2, 2.5) * mm});
            skLineSegment(sketch, "E680", {"start": v(-0.2, 2.5) * mm, "end": v(-0.52, 2.48) * mm});
            skLineSegment(sketch, "E681", {"start": v(-0.52, 2.48) * mm, "end": v(-0.84, 2.41) * mm});
            skLineSegment(sketch, "E682", {"start": v(-0.84, 2.41) * mm, "end": v(-1.15, 2.3) * mm});
            skLineSegment(sketch, "E683", {"start": v(-1.15, 2.3) * mm, "end": v(-1.44, 2.17) * mm});
            skLineSegment(sketch, "E684", {"start": v(-1.44, 2.17) * mm, "end": v(-1.72, 1.98) * mm});
            skLineSegment(sketch, "E685", {"start": v(-1.72, 1.98) * mm, "end": v(-1.96, 1.77) * mm});
            skLineSegment(sketch, "E686", {"start": v(-1.96, 1.77) * mm, "end": v(-2.18, 1.52) * mm});
            skLineSegment(sketch, "E687", {"start": v(-2.18, 1.52) * mm, "end": v(-2.36, 1.25) * mm});
            skLineSegment(sketch, "E688", {"start": v(-2.36, 1.25) * mm, "end": v(-2.5, 0.96) * mm});
            skLineSegment(sketch, "E689", {"start": v(-2.5, 0.96) * mm, "end": v(-2.6, 0.65) * mm});
            skLineSegment(sketch, "E690", {"start": v(-2.6, 0.65) * mm, "end": v(-2.67, 0.33) * mm});
            skLineSegment(sketch, "E691", {"start": v(-2.67, 0.33) * mm, "end": v(-2.7, 0) * mm});
            skLineSegment(sketch, "E692", {"start": v(-2.7, 0) * mm, "end": v(-2.67, -0.33) * mm});
            skLineSegment(sketch, "E693", {"start": v(-2.67, -0.33) * mm, "end": v(-2.6, -0.65) * mm});
            skLineSegment(sketch, "E694", {"start": v(-2.6, -0.65) * mm, "end": v(-2.5, -0.96) * mm});
            skLineSegment(sketch, "E695", {"start": v(-2.5, -0.96) * mm, "end": v(-2.36, -1.25) * mm});
            skLineSegment(sketch, "E696", {"start": v(-2.36, -1.25) * mm, "end": v(-2.18, -1.52) * mm});
            skLineSegment(sketch, "E697", {"start": v(-2.18, -1.52) * mm, "end": v(-1.96, -1.77) * mm});
            skLineSegment(sketch, "E698", {"start": v(-1.96, -1.77) * mm, "end": v(-1.72, -1.98) * mm});
            skLineSegment(sketch, "E699", {"start": v(-1.72, -1.98) * mm, "end": v(-1.44, -2.17) * mm});
            skLineSegment(sketch, "E700", {"start": v(-1.44, -2.17) * mm, "end": v(-1.15, -2.3) * mm});
            skLineSegment(sketch, "E701", {"start": v(-1.15, -2.3) * mm, "end": v(-0.84, -2.41) * mm});
            skLineSegment(sketch, "E702", {"start": v(-0.84, -2.41) * mm, "end": v(-0.52, -2.48) * mm});
            skLineSegment(sketch, "E703", {"start": v(-0.52, -2.48) * mm, "end": v(-0.2, -2.5) * mm});
            skLineSegment(sketch, "E704", {"start": v(-0.2, -2.5) * mm, "end": v(0.13, -2.48) * mm});
            skLineSegment(sketch, "E705", {"start": v(0.13, -2.48) * mm, "end": v(0.45, -2.41) * mm});
            skLineSegment(sketch, "E706", {"start": v(0.45, -2.41) * mm, "end": v(0.76, -2.3) * mm});
            skLineSegment(sketch, "E707", {"start": v(0.76, -2.3) * mm, "end": v(1.06, -2.17) * mm});
            skLineSegment(sketch, "E708", {"start": v(1.06, -2.17) * mm, "end": v(1.33, -1.98) * mm});
            skLineSegment(sketch, "E709", {"start": v(1.33, -1.98) * mm, "end": v(1.57, -1.77) * mm});
            skLineSegment(sketch, "E710", {"start": v(1.57, -1.77) * mm, "end": v(1.79, -1.52) * mm});
            skLineSegment(sketch, "E711", {"start": v(1.79, -1.52) * mm, "end": v(1.97, -1.25) * mm});
            skLineSegment(sketch, "E712", {"start": v(1.97, -1.25) * mm, "end": v(2.12, -0.96) * mm});
            skLineSegment(sketch, "E713", {"start": v(2.12, -0.96) * mm, "end": v(2.22, -0.65) * mm});
            skLineSegment(sketch, "E714", {"start": v(2.22, -0.65) * mm, "end": v(2.29, -0.33) * mm});
            skLineSegment(sketch, "E715", {"start": v(2.29, -0.33) * mm, "end": v(2.3, 0) * mm});
            skSolve(sketch);
        }
        {
            var Q0;
            Q0 = qSketchRegion(id + "F4", true);
            extrude(context, id + "F5", {"entities" : qUnion([Q0]), "depth" : 4 * mm});
        }
        {
            var Q0;
            Q0=qCreatedBy(makeId("Front.planeOp"),FACE);
            var sketch = newSketch(context, id + "F6", { "sketchPlane" : qUnion([Q0])});
            skLineSegment(sketch, "E716", {"start": v(19.68, -7.7) * mm, "end": v(18.9, -6.8) * mm});
            skLineSegment(sketch, "E717", {"start": v(18.9, -6.8) * mm, "end": v(18.2, -6.15) * mm});
            skLineSegment(sketch, "E718", {"start": v(18.2, -6.15) * mm, "end": v(17.65, -5.76) * mm});
            skLineSegment(sketch, "E719", {"start": v(17.65, -5.76) * mm, "end": v(17.3, -5.57) * mm});
            skLineSegment(sketch, "E720", {"start": v(17.3, -5.57) * mm, "end": v(15.36, -4.94) * mm});
            skLineSegment(sketch, "E721", {"start": v(15.36, -4.94) * mm, "end": v(15.19, -4.83) * mm});
            skLineSegment(sketch, "E722", {"start": v(15.19, -4.83) * mm, "end": v(15.1, -4.65) * mm});
            skLineSegment(sketch, "E723", {"start": v(15.1, -4.65) * mm, "end": v(15.1, -4.44) * mm});
            skLineSegment(sketch, "E724", {"start": v(15.1, -4.44) * mm, "end": v(15.6, -2.14) * mm});
            skLineSegment(sketch, "E725", {"start": v(15.6, -2.14) * mm, "end": v(15.67, -1.95) * mm});
            skLineSegment(sketch, "E726", {"start": v(15.67, -1.95) * mm, "end": v(15.83, -1.82) * mm});
            skLineSegment(sketch, "E727", {"start": v(15.83, -1.82) * mm, "end": v(16.03, -1.79) * mm});
            skLineSegment(sketch, "E728", {"start": v(16.03, -1.79) * mm, "end": v(18.05, -2) * mm});
            skLineSegment(sketch, "E729", {"start": v(18.05, -2) * mm, "end": v(18.46, -1.97) * mm});
            skLineSegment(sketch, "E730", {"start": v(18.46, -1.97) * mm, "end": v(19.12, -1.84) * mm});
            skLineSegment(sketch, "E731", {"start": v(19.12, -1.84) * mm, "end": v(20.02, -1.54) * mm});
            skLineSegment(sketch, "E732", {"start": v(20.02, -1.54) * mm, "end": v(21.1, -1.03) * mm});
            skLineSegment(sketch, "E733", {"start": v(21.1, -1.03) * mm, "end": v(21.1, 1.03) * mm});
            skLineSegment(sketch, "E734", {"start": v(21.1, 1.03) * mm, "end": v(20.02, 1.54) * mm});
            skLineSegment(sketch, "E735", {"start": v(20.02, 1.54) * mm, "end": v(19.12, 1.84) * mm});
            skLineSegment(sketch, "E736", {"start": v(19.12, 1.84) * mm, "end": v(18.46, 1.97) * mm});
            skLineSegment(sketch, "E737", {"start": v(18.46, 1.97) * mm, "end": v(18.05, 2) * mm});
            skLineSegment(sketch, "E738", {"start": v(18.05, 2) * mm, "end": v(16.03, 1.79) * mm});
            skLineSegment(sketch, "E739", {"start": v(16.03, 1.79) * mm, "end": v(15.83, 1.82) * mm});
            skLineSegment(sketch, "E740", {"start": v(15.83, 1.82) * mm, "end": v(15.67, 1.95) * mm});
            skLineSegment(sketch, "E741", {"start": v(15.67, 1.95) * mm, "end": v(15.6, 2.14) * mm});
            skLineSegment(sketch, "E742", {"start": v(15.6, 2.14) * mm, "end": v(15.1, 4.44) * mm});
            skLineSegment(sketch, "E743", {"start": v(15.1, 4.44) * mm, "end": v(15.1, 4.65) * mm});
            skLineSegment(sketch, "E744", {"start": v(15.1, 4.65) * mm, "end": v(15.19, 4.83) * mm});
            skLineSegment(sketch, "E745", {"start": v(15.19, 4.83) * mm, "end": v(15.36, 4.94) * mm});
            skLineSegment(sketch, "E746", {"start": v(15.36, 4.94) * mm, "end": v(17.3, 5.57) * mm});
            skLineSegment(sketch, "E747", {"start": v(17.3, 5.57) * mm, "end": v(17.65, 5.76) * mm});
            skLineSegment(sketch, "E748", {"start": v(17.65, 5.76) * mm, "end": v(18.2, 6.15) * mm});
            skLineSegment(sketch, "E749", {"start": v(18.2, 6.15) * mm, "end": v(18.9, 6.8) * mm});
            skLineSegment(sketch, "E750", {"start": v(18.9, 6.8) * mm, "end": v(19.68, 7.7) * mm});
            skLineSegment(sketch, "E751", {"start": v(19.68, 7.7) * mm, "end": v(18.85, 9.57) * mm});
            skLineSegment(sketch, "E752", {"start": v(18.85, 9.57) * mm, "end": v(17.65, 9.6) * mm});
            skLineSegment(sketch, "E753", {"start": v(17.65, 9.6) * mm, "end": v(16.71, 9.5) * mm});
            skLineSegment(sketch, "E754", {"start": v(16.71, 9.5) * mm, "end": v(16.05, 9.36) * mm});
            skLineSegment(sketch, "E755", {"start": v(16.05, 9.36) * mm, "end": v(15.67, 9.22) * mm});
            skLineSegment(sketch, "E756", {"start": v(15.67, 9.22) * mm, "end": v(13.9, 8.2) * mm});
            skLineSegment(sketch, "E757", {"start": v(13.9, 8.2) * mm, "end": v(13.7, 8.15) * mm});
            skLineSegment(sketch, "E758", {"start": v(13.7, 8.15) * mm, "end": v(13.51, 8.2) * mm});
            skLineSegment(sketch, "E759", {"start": v(13.51, 8.2) * mm, "end": v(13.37, 8.34) * mm});
            skLineSegment(sketch, "E760", {"start": v(13.37, 8.34) * mm, "end": v(11.98, 10.25) * mm});
            skLineSegment(sketch, "E761", {"start": v(11.98, 10.25) * mm, "end": v(11.89, 10.43) * mm});
            skLineSegment(sketch, "E762", {"start": v(11.89, 10.43) * mm, "end": v(11.9, 10.64) * mm});
            skLineSegment(sketch, "E763", {"start": v(11.9, 10.64) * mm, "end": v(12.01, 10.8) * mm});
            skLineSegment(sketch, "E764", {"start": v(12.01, 10.8) * mm, "end": v(13.53, 12.17) * mm});
            skLineSegment(sketch, "E765", {"start": v(13.53, 12.17) * mm, "end": v(13.77, 12.5) * mm});
            skLineSegment(sketch, "E766", {"start": v(13.77, 12.5) * mm, "end": v(14.12, 13.07) * mm});
            skLineSegment(sketch, "E767", {"start": v(14.12, 13.07) * mm, "end": v(14.5, 13.94) * mm});
            skLineSegment(sketch, "E768", {"start": v(14.5, 13.94) * mm, "end": v(14.84, 15.09) * mm});
            skLineSegment(sketch, "E769", {"start": v(14.84, 15.09) * mm, "end": v(13.31, 16.46) * mm});
            skLineSegment(sketch, "E770", {"start": v(13.31, 16.46) * mm, "end": v(12.21, 16) * mm});
            skLineSegment(sketch, "E771", {"start": v(12.21, 16) * mm, "end": v(11.39, 15.53) * mm});
            skLineSegment(sketch, "E772", {"start": v(11.39, 15.53) * mm, "end": v(10.85, 15.13) * mm});
            skLineSegment(sketch, "E773", {"start": v(10.85, 15.13) * mm, "end": v(10.55, 14.85) * mm});
            skLineSegment(sketch, "E774", {"start": v(10.55, 14.85) * mm, "end": v(9.35, 13.2) * mm});
            skLineSegment(sketch, "E775", {"start": v(9.35, 13.2) * mm, "end": v(9.2, 13.07) * mm});
            skLineSegment(sketch, "E776", {"start": v(9.2, 13.07) * mm, "end": v(9, 13.04) * mm});
            skLineSegment(sketch, "E777", {"start": v(9, 13.04) * mm, "end": v(8.8, 13.1) * mm});
            skLineSegment(sketch, "E778", {"start": v(8.8, 13.1) * mm, "end": v(6.76, 14.29) * mm});
            skLineSegment(sketch, "E779", {"start": v(6.76, 14.29) * mm, "end": v(6.6, 14.42) * mm});
            skLineSegment(sketch, "E780", {"start": v(6.6, 14.42) * mm, "end": v(6.53, 14.6) * mm});
            skLineSegment(sketch, "E781", {"start": v(6.53, 14.6) * mm, "end": v(6.57, 14.8) * mm});
            skLineSegment(sketch, "E782", {"start": v(6.57, 14.8) * mm, "end": v(7.4, 16.67) * mm});
            skLineSegment(sketch, "E783", {"start": v(7.4, 16.67) * mm, "end": v(7.5, 17.06) * mm});
            skLineSegment(sketch, "E784", {"start": v(7.5, 17.06) * mm, "end": v(7.57, 17.74) * mm});
            skLineSegment(sketch, "E785", {"start": v(7.57, 17.74) * mm, "end": v(7.56, 18.69) * mm});
            skLineSegment(sketch, "E786", {"start": v(7.56, 18.69) * mm, "end": v(7.41, 19.87) * mm});
            skLineSegment(sketch, "E787", {"start": v(7.41, 19.87) * mm, "end": v(5.46, 20.5) * mm});
            skLineSegment(sketch, "E788", {"start": v(5.46, 20.5) * mm, "end": v(4.64, 19.63) * mm});
            skLineSegment(sketch, "E789", {"start": v(4.64, 19.63) * mm, "end": v(4.08, 18.87) * mm});
            skLineSegment(sketch, "E790", {"start": v(4.08, 18.87) * mm, "end": v(3.74, 18.28) * mm});
            skLineSegment(sketch, "E791", {"start": v(3.74, 18.28) * mm, "end": v(3.59, 17.9) * mm});
            skLineSegment(sketch, "E792", {"start": v(3.59, 17.9) * mm, "end": v(3.17, 15.91) * mm});
            skLineSegment(sketch, "E793", {"start": v(3.17, 15.91) * mm, "end": v(3.07, 15.73) * mm});
            skLineSegment(sketch, "E794", {"start": v(3.07, 15.73) * mm, "end": v(2.9, 15.62) * mm});
            skLineSegment(sketch, "E795", {"start": v(2.9, 15.62) * mm, "end": v(2.7, 15.6) * mm});
            skLineSegment(sketch, "E796", {"start": v(2.7, 15.6) * mm, "end": v(0.36, 15.86) * mm});
            skLineSegment(sketch, "E797", {"start": v(0.36, 15.86) * mm, "end": v(0.16, 15.9) * mm});
            skLineSegment(sketch, "E798", {"start": v(0.16, 15.9) * mm, "end": v(0.02, 16.05) * mm});
            skLineSegment(sketch, "E799", {"start": v(0.02, 16.05) * mm, "end": v(-0.03, 16.25) * mm});
            skLineSegment(sketch, "E800", {"start": v(-0.03, 16.25) * mm, "end": v(-0.03, 18.29) * mm});
            skLineSegment(sketch, "E801", {"start": v(-0.03, 18.29) * mm, "end": v(-0.1, 18.69) * mm});
            skLineSegment(sketch, "E802", {"start": v(-0.1, 18.69) * mm, "end": v(-0.31, 19.33) * mm});
            skLineSegment(sketch, "E803", {"start": v(-0.31, 19.33) * mm, "end": v(-0.7, 20.2) * mm});
            skLineSegment(sketch, "E804", {"start": v(-0.7, 20.2) * mm, "end": v(-1.32, 21.22) * mm});
            skLineSegment(sketch, "E805", {"start": v(-1.32, 21.22) * mm, "end": v(-3.37, 21) * mm});
            skLineSegment(sketch, "E806", {"start": v(-3.37, 21) * mm, "end": v(-3.76, 19.87) * mm});
            skLineSegment(sketch, "E807", {"start": v(-3.76, 19.87) * mm, "end": v(-3.96, 18.95) * mm});
            skLineSegment(sketch, "E808", {"start": v(-3.96, 18.95) * mm, "end": v(-4.03, 18.28) * mm});
            skLineSegment(sketch, "E809", {"start": v(-4.03, 18.28) * mm, "end": v(-4.02, 17.87) * mm});
            skLineSegment(sketch, "E810", {"start": v(-4.02, 17.87) * mm, "end": v(-3.6, 15.88) * mm});
            skLineSegment(sketch, "E811", {"start": v(-3.6, 15.88) * mm, "end": v(-3.6, 15.67) * mm});
            skLineSegment(sketch, "E812", {"start": v(-3.6, 15.67) * mm, "end": v(-3.71, 15.5) * mm});
            skLineSegment(sketch, "E813", {"start": v(-3.71, 15.5) * mm, "end": v(-3.9, 15.4) * mm});
            skLineSegment(sketch, "E814", {"start": v(-3.9, 15.4) * mm, "end": v(-6.14, 14.68) * mm});
            skLineSegment(sketch, "E815", {"start": v(-6.14, 14.68) * mm, "end": v(-6.34, 14.65) * mm});
            skLineSegment(sketch, "E816", {"start": v(-6.34, 14.65) * mm, "end": v(-6.53, 14.72) * mm});
            skLineSegment(sketch, "E817", {"start": v(-6.53, 14.72) * mm, "end": v(-6.65, 14.88) * mm});
            skLineSegment(sketch, "E818", {"start": v(-6.65, 14.88) * mm, "end": v(-7.48, 16.74) * mm});
            skLineSegment(sketch, "E819", {"start": v(-7.48, 16.74) * mm, "end": v(-7.71, 17.08) * mm});
            skLineSegment(sketch, "E820", {"start": v(-7.71, 17.08) * mm, "end": v(-8.16, 17.59) * mm});
            skLineSegment(sketch, "E821", {"start": v(-8.16, 17.59) * mm, "end": v(-8.87, 18.22) * mm});
            skLineSegment(sketch, "E822", {"start": v(-8.87, 18.22) * mm, "end": v(-9.85, 18.9) * mm});
            skLineSegment(sketch, "E823", {"start": v(-9.85, 18.9) * mm, "end": v(-11.63, 17.87) * mm});
            skLineSegment(sketch, "E824", {"start": v(-11.63, 17.87) * mm, "end": v(-11.53, 16.68) * mm});
            skLineSegment(sketch, "E825", {"start": v(-11.53, 16.68) * mm, "end": v(-11.34, 15.75) * mm});
            skLineSegment(sketch, "E826", {"start": v(-11.34, 15.75) * mm, "end": v(-11.12, 15.1) * mm});
            skLineSegment(sketch, "E827", {"start": v(-11.12, 15.1) * mm, "end": v(-10.95, 14.74) * mm});
            skLineSegment(sketch, "E828", {"start": v(-10.95, 14.74) * mm, "end": v(-9.75, 13.1) * mm});
            skLineSegment(sketch, "E829", {"start": v(-9.75, 13.1) * mm, "end": v(-9.68, 12.9) * mm});
            skLineSegment(sketch, "E830", {"start": v(-9.68, 12.9) * mm, "end": v(-9.7, 12.7) * mm});
            skLineSegment(sketch, "E831", {"start": v(-9.7, 12.7) * mm, "end": v(-9.83, 12.54) * mm});
            skLineSegment(sketch, "E832", {"start": v(-9.83, 12.54) * mm, "end": v(-11.59, 10.97) * mm});
            skLineSegment(sketch, "E833", {"start": v(-11.59, 10.97) * mm, "end": v(-11.76, 10.86) * mm});
            skLineSegment(sketch, "E834", {"start": v(-11.76, 10.86) * mm, "end": v(-11.96, 10.85) * mm});
            skLineSegment(sketch, "E835", {"start": v(-11.96, 10.85) * mm, "end": v(-12.14, 10.94) * mm});
            skLineSegment(sketch, "E836", {"start": v(-12.14, 10.94) * mm, "end": v(-13.65, 12.3) * mm});
            skLineSegment(sketch, "E837", {"start": v(-13.65, 12.3) * mm, "end": v(-14, 12.52) * mm});
            skLineSegment(sketch, "E838", {"start": v(-14, 12.52) * mm, "end": v(-14.62, 12.8) * mm});
            skLineSegment(sketch, "E839", {"start": v(-14.62, 12.8) * mm, "end": v(-15.52, 13.08) * mm});
            skLineSegment(sketch, "E840", {"start": v(-15.52, 13.08) * mm, "end": v(-16.7, 13.3) * mm});
            skLineSegment(sketch, "E841", {"start": v(-16.7, 13.3) * mm, "end": v(-17.9, 11.64) * mm});
            skLineSegment(sketch, "E842", {"start": v(-17.9, 11.64) * mm, "end": v(-17.33, 10.6) * mm});
            skLineSegment(sketch, "E843", {"start": v(-17.33, 10.6) * mm, "end": v(-16.77, 9.83) * mm});
            skLineSegment(sketch, "E844", {"start": v(-16.77, 9.83) * mm, "end": v(-16.32, 9.33) * mm});
            skLineSegment(sketch, "E845", {"start": v(-16.32, 9.33) * mm, "end": v(-16, 9.07) * mm});
            skLineSegment(sketch, "E846", {"start": v(-16, 9.07) * mm, "end": v(-14.24, 8.05) * mm});
            skLineSegment(sketch, "E847", {"start": v(-14.24, 8.05) * mm, "end": v(-14.1, 7.9) * mm});
            skLineSegment(sketch, "E848", {"start": v(-14.1, 7.9) * mm, "end": v(-14.04, 7.7) * mm});
            skLineSegment(sketch, "E849", {"start": v(-14.04, 7.7) * mm, "end": v(-14.1, 7.51) * mm});
            skLineSegment(sketch, "E850", {"start": v(-14.1, 7.51) * mm, "end": v(-15.06, 5.36) * mm});
            skLineSegment(sketch, "E851", {"start": v(-15.06, 5.36) * mm, "end": v(-15.17, 5.19) * mm});
            skLineSegment(sketch, "E852", {"start": v(-15.17, 5.19) * mm, "end": v(-15.35, 5.1) * mm});
            skLineSegment(sketch, "E853", {"start": v(-15.35, 5.1) * mm, "end": v(-15.55, 5.1) * mm});
            skLineSegment(sketch, "E854", {"start": v(-15.55, 5.1) * mm, "end": v(-17.49, 5.74) * mm});
            skLineSegment(sketch, "E855", {"start": v(-17.49, 5.74) * mm, "end": v(-17.9, 5.79) * mm});
            skLineSegment(sketch, "E856", {"start": v(-17.9, 5.79) * mm, "end": v(-18.57, 5.8) * mm});
            skLineSegment(sketch, "E857", {"start": v(-18.57, 5.8) * mm, "end": v(-19.51, 5.7) * mm});
            skLineSegment(sketch, "E858", {"start": v(-19.51, 5.7) * mm, "end": v(-20.67, 5.42) * mm});
            skLineSegment(sketch, "E859", {"start": v(-20.67, 5.42) * mm, "end": v(-21.1, 3.4) * mm});
            skLineSegment(sketch, "E860", {"start": v(-21.1, 3.4) * mm, "end": v(-20.15, 2.69) * mm});
            skLineSegment(sketch, "E861", {"start": v(-20.15, 2.69) * mm, "end": v(-19.33, 2.2) * mm});
            skLineSegment(sketch, "E862", {"start": v(-19.33, 2.2) * mm, "end": v(-18.71, 1.94) * mm});
            skLineSegment(sketch, "E863", {"start": v(-18.71, 1.94) * mm, "end": v(-18.32, 1.82) * mm});
            skLineSegment(sketch, "E864", {"start": v(-18.32, 1.82) * mm, "end": v(-16.3, 1.6) * mm});
            skLineSegment(sketch, "E865", {"start": v(-16.3, 1.6) * mm, "end": v(-16.1, 1.54) * mm});
            skLineSegment(sketch, "E866", {"start": v(-16.1, 1.54) * mm, "end": v(-15.98, 1.38) * mm});
            skLineSegment(sketch, "E867", {"start": v(-15.98, 1.38) * mm, "end": v(-15.94, 1.18) * mm});
            skLineSegment(sketch, "E868", {"start": v(-15.94, 1.18) * mm, "end": v(-15.94, -1.18) * mm});
            skLineSegment(sketch, "E869", {"start": v(-15.94, -1.18) * mm, "end": v(-15.98, -1.38) * mm});
            skLineSegment(sketch, "E870", {"start": v(-15.98, -1.38) * mm, "end": v(-16.1, -1.54) * mm});
            skLineSegment(sketch, "E871", {"start": v(-16.1, -1.54) * mm, "end": v(-16.3, -1.6) * mm});
            skLineSegment(sketch, "E872", {"start": v(-16.3, -1.6) * mm, "end": v(-18.32, -1.82) * mm});
            skLineSegment(sketch, "E873", {"start": v(-18.32, -1.82) * mm, "end": v(-18.71, -1.94) * mm});
            skLineSegment(sketch, "E874", {"start": v(-18.71, -1.94) * mm, "end": v(-19.33, -2.2) * mm});
            skLineSegment(sketch, "E875", {"start": v(-19.33, -2.2) * mm, "end": v(-20.15, -2.69) * mm});
            skLineSegment(sketch, "E876", {"start": v(-20.15, -2.69) * mm, "end": v(-21.1, -3.4) * mm});
            skLineSegment(sketch, "E877", {"start": v(-21.1, -3.4) * mm, "end": v(-20.67, -5.42) * mm});
            skLineSegment(sketch, "E878", {"start": v(-20.67, -5.42) * mm, "end": v(-19.51, -5.7) * mm});
            skLineSegment(sketch, "E879", {"start": v(-19.51, -5.7) * mm, "end": v(-18.57, -5.8) * mm});
            skLineSegment(sketch, "E880", {"start": v(-18.57, -5.8) * mm, "end": v(-17.9, -5.79) * mm});
            skLineSegment(sketch, "E881", {"start": v(-17.9, -5.79) * mm, "end": v(-17.49, -5.74) * mm});
            skLineSegment(sketch, "E882", {"start": v(-17.49, -5.74) * mm, "end": v(-15.55, -5.1) * mm});
            skLineSegment(sketch, "E883", {"start": v(-15.55, -5.1) * mm, "end": v(-15.35, -5.1) * mm});
            skLineSegment(sketch, "E884", {"start": v(-15.35, -5.1) * mm, "end": v(-15.17, -5.19) * mm});
            skLineSegment(sketch, "E885", {"start": v(-15.17, -5.19) * mm, "end": v(-15.06, -5.36) * mm});
            skLineSegment(sketch, "E886", {"start": v(-15.06, -5.36) * mm, "end": v(-14.1, -7.51) * mm});
            skLineSegment(sketch, "E887", {"start": v(-14.1, -7.51) * mm, "end": v(-14.04, -7.7) * mm});
            skLineSegment(sketch, "E888", {"start": v(-14.04, -7.7) * mm, "end": v(-14.1, -7.9) * mm});
            skLineSegment(sketch, "E889", {"start": v(-14.1, -7.9) * mm, "end": v(-14.24, -8.05) * mm});
            skLineSegment(sketch, "E890", {"start": v(-14.24, -8.05) * mm, "end": v(-16, -9.07) * mm});
            skLineSegment(sketch, "E891", {"start": v(-16, -9.07) * mm, "end": v(-16.32, -9.33) * mm});
            skLineSegment(sketch, "E892", {"start": v(-16.32, -9.33) * mm, "end": v(-16.77, -9.83) * mm});
            skLineSegment(sketch, "E893", {"start": v(-16.77, -9.83) * mm, "end": v(-17.33, -10.6) * mm});
            skLineSegment(sketch, "E894", {"start": v(-17.33, -10.6) * mm, "end": v(-17.9, -11.64) * mm});
            skLineSegment(sketch, "E895", {"start": v(-17.9, -11.64) * mm, "end": v(-16.7, -13.3) * mm});
            skLineSegment(sketch, "E896", {"start": v(-16.7, -13.3) * mm, "end": v(-15.52, -13.08) * mm});
            skLineSegment(sketch, "E897", {"start": v(-15.52, -13.08) * mm, "end": v(-14.62, -12.8) * mm});
            skLineSegment(sketch, "E898", {"start": v(-14.62, -12.8) * mm, "end": v(-14, -12.52) * mm});
            skLineSegment(sketch, "E899", {"start": v(-14, -12.52) * mm, "end": v(-13.65, -12.3) * mm});
            skLineSegment(sketch, "E900", {"start": v(-13.65, -12.3) * mm, "end": v(-12.14, -10.94) * mm});
            skLineSegment(sketch, "E901", {"start": v(-12.14, -10.94) * mm, "end": v(-11.96, -10.85) * mm});
            skLineSegment(sketch, "E902", {"start": v(-11.96, -10.85) * mm, "end": v(-11.76, -10.86) * mm});
            skLineSegment(sketch, "E903", {"start": v(-11.76, -10.86) * mm, "end": v(-11.59, -10.97) * mm});
            skLineSegment(sketch, "E904", {"start": v(-11.59, -10.97) * mm, "end": v(-9.83, -12.54) * mm});
            skLineSegment(sketch, "E905", {"start": v(-9.83, -12.54) * mm, "end": v(-9.7, -12.7) * mm});
            skLineSegment(sketch, "E906", {"start": v(-9.7, -12.7) * mm, "end": v(-9.68, -12.9) * mm});
            skLineSegment(sketch, "E907", {"start": v(-9.68, -12.9) * mm, "end": v(-9.75, -13.1) * mm});
            skLineSegment(sketch, "E908", {"start": v(-9.75, -13.1) * mm, "end": v(-10.95, -14.74) * mm});
            skLineSegment(sketch, "E909", {"start": v(-10.95, -14.74) * mm, "end": v(-11.12, -15.1) * mm});
            skLineSegment(sketch, "E910", {"start": v(-11.12, -15.1) * mm, "end": v(-11.34, -15.75) * mm});
            skLineSegment(sketch, "E911", {"start": v(-11.34, -15.75) * mm, "end": v(-11.53, -16.68) * mm});
            skLineSegment(sketch, "E912", {"start": v(-11.53, -16.68) * mm, "end": v(-11.63, -17.87) * mm});
            skLineSegment(sketch, "E913", {"start": v(-11.63, -17.87) * mm, "end": v(-9.85, -18.9) * mm});
            skLineSegment(sketch, "E914", {"start": v(-9.85, -18.9) * mm, "end": v(-8.87, -18.22) * mm});
            skLineSegment(sketch, "E915", {"start": v(-8.87, -18.22) * mm, "end": v(-8.16, -17.59) * mm});
            skLineSegment(sketch, "E916", {"start": v(-8.16, -17.59) * mm, "end": v(-7.71, -17.08) * mm});
            skLineSegment(sketch, "E917", {"start": v(-7.71, -17.08) * mm, "end": v(-7.48, -16.74) * mm});
            skLineSegment(sketch, "E918", {"start": v(-7.48, -16.74) * mm, "end": v(-6.65, -14.88) * mm});
            skLineSegment(sketch, "E919", {"start": v(-6.65, -14.88) * mm, "end": v(-6.53, -14.72) * mm});
            skLineSegment(sketch, "E920", {"start": v(-6.53, -14.72) * mm, "end": v(-6.34, -14.65) * mm});
            skLineSegment(sketch, "E921", {"start": v(-6.34, -14.65) * mm, "end": v(-6.14, -14.68) * mm});
            skLineSegment(sketch, "E922", {"start": v(-6.14, -14.68) * mm, "end": v(-3.9, -15.4) * mm});
            skLineSegment(sketch, "E923", {"start": v(-3.9, -15.4) * mm, "end": v(-3.71, -15.5) * mm});
            skLineSegment(sketch, "E924", {"start": v(-3.71, -15.5) * mm, "end": v(-3.6, -15.67) * mm});
            skLineSegment(sketch, "E925", {"start": v(-3.6, -15.67) * mm, "end": v(-3.6, -15.88) * mm});
            skLineSegment(sketch, "E926", {"start": v(-3.6, -15.88) * mm, "end": v(-4.02, -17.87) * mm});
            skLineSegment(sketch, "E927", {"start": v(-4.02, -17.87) * mm, "end": v(-4.03, -18.28) * mm});
            skLineSegment(sketch, "E928", {"start": v(-4.03, -18.28) * mm, "end": v(-3.96, -18.95) * mm});
            skLineSegment(sketch, "E929", {"start": v(-3.96, -18.95) * mm, "end": v(-3.76, -19.87) * mm});
            skLineSegment(sketch, "E930", {"start": v(-3.76, -19.87) * mm, "end": v(-3.37, -21) * mm});
            skLineSegment(sketch, "E931", {"start": v(-3.37, -21) * mm, "end": v(-1.32, -21.22) * mm});
            skLineSegment(sketch, "E932", {"start": v(-1.32, -21.22) * mm, "end": v(-0.7, -20.2) * mm});
            skLineSegment(sketch, "E933", {"start": v(-0.7, -20.2) * mm, "end": v(-0.31, -19.33) * mm});
            skLineSegment(sketch, "E934", {"start": v(-0.31, -19.33) * mm, "end": v(-0.1, -18.69) * mm});
            skLineSegment(sketch, "E935", {"start": v(-0.1, -18.69) * mm, "end": v(-0.03, -18.29) * mm});
            skLineSegment(sketch, "E936", {"start": v(-0.03, -18.29) * mm, "end": v(-0.03, -16.25) * mm});
            skLineSegment(sketch, "E937", {"start": v(-0.03, -16.25) * mm, "end": v(0.02, -16.05) * mm});
            skLineSegment(sketch, "E938", {"start": v(0.02, -16.05) * mm, "end": v(0.16, -15.9) * mm});
            skLineSegment(sketch, "E939", {"start": v(0.16, -15.9) * mm, "end": v(0.36, -15.86) * mm});
            skLineSegment(sketch, "E940", {"start": v(0.36, -15.86) * mm, "end": v(2.7, -15.6) * mm});
            skLineSegment(sketch, "E941", {"start": v(2.7, -15.6) * mm, "end": v(2.9, -15.62) * mm});
            skLineSegment(sketch, "E942", {"start": v(2.9, -15.62) * mm, "end": v(3.07, -15.73) * mm});
            skLineSegment(sketch, "E943", {"start": v(3.07, -15.73) * mm, "end": v(3.17, -15.91) * mm});
            skLineSegment(sketch, "E944", {"start": v(3.17, -15.91) * mm, "end": v(3.59, -17.9) * mm});
            skLineSegment(sketch, "E945", {"start": v(3.59, -17.9) * mm, "end": v(3.74, -18.28) * mm});
            skLineSegment(sketch, "E946", {"start": v(3.74, -18.28) * mm, "end": v(4.08, -18.87) * mm});
            skLineSegment(sketch, "E947", {"start": v(4.08, -18.87) * mm, "end": v(4.64, -19.63) * mm});
            skLineSegment(sketch, "E948", {"start": v(4.64, -19.63) * mm, "end": v(5.46, -20.5) * mm});
            skLineSegment(sketch, "E949", {"start": v(5.46, -20.5) * mm, "end": v(7.41, -19.87) * mm});
            skLineSegment(sketch, "E950", {"start": v(7.41, -19.87) * mm, "end": v(7.56, -18.69) * mm});
            skLineSegment(sketch, "E951", {"start": v(7.56, -18.69) * mm, "end": v(7.57, -17.74) * mm});
            skLineSegment(sketch, "E952", {"start": v(7.57, -17.74) * mm, "end": v(7.5, -17.06) * mm});
            skLineSegment(sketch, "E953", {"start": v(7.5, -17.06) * mm, "end": v(7.4, -16.67) * mm});
            skLineSegment(sketch, "E954", {"start": v(7.4, -16.67) * mm, "end": v(6.57, -14.8) * mm});
            skLineSegment(sketch, "E955", {"start": v(6.57, -14.8) * mm, "end": v(6.53, -14.6) * mm});
            skLineSegment(sketch, "E956", {"start": v(6.53, -14.6) * mm, "end": v(6.6, -14.42) * mm});
            skLineSegment(sketch, "E957", {"start": v(6.6, -14.42) * mm, "end": v(6.76, -14.29) * mm});
            skLineSegment(sketch, "E958", {"start": v(6.76, -14.29) * mm, "end": v(8.8, -13.1) * mm});
            skLineSegment(sketch, "E959", {"start": v(8.8, -13.1) * mm, "end": v(9, -13.04) * mm});
            skLineSegment(sketch, "E960", {"start": v(9, -13.04) * mm, "end": v(9.2, -13.07) * mm});
            skLineSegment(sketch, "E961", {"start": v(9.2, -13.07) * mm, "end": v(9.35, -13.2) * mm});
            skLineSegment(sketch, "E962", {"start": v(9.35, -13.2) * mm, "end": v(10.55, -14.85) * mm});
            skLineSegment(sketch, "E963", {"start": v(10.55, -14.85) * mm, "end": v(10.85, -15.13) * mm});
            skLineSegment(sketch, "E964", {"start": v(10.85, -15.13) * mm, "end": v(11.39, -15.53) * mm});
            skLineSegment(sketch, "E965", {"start": v(11.39, -15.53) * mm, "end": v(12.21, -16) * mm});
            skLineSegment(sketch, "E966", {"start": v(12.21, -16) * mm, "end": v(13.31, -16.46) * mm});
            skLineSegment(sketch, "E967", {"start": v(13.31, -16.46) * mm, "end": v(14.84, -15.09) * mm});
            skLineSegment(sketch, "E968", {"start": v(14.84, -15.09) * mm, "end": v(14.5, -13.94) * mm});
            skLineSegment(sketch, "E969", {"start": v(14.5, -13.94) * mm, "end": v(14.12, -13.07) * mm});
            skLineSegment(sketch, "E970", {"start": v(14.12, -13.07) * mm, "end": v(13.77, -12.5) * mm});
            skLineSegment(sketch, "E971", {"start": v(13.77, -12.5) * mm, "end": v(13.53, -12.17) * mm});
            skLineSegment(sketch, "E972", {"start": v(13.53, -12.17) * mm, "end": v(12.01, -10.8) * mm});
            skLineSegment(sketch, "E973", {"start": v(12.01, -10.8) * mm, "end": v(11.9, -10.64) * mm});
            skLineSegment(sketch, "E974", {"start": v(11.9, -10.64) * mm, "end": v(11.89, -10.43) * mm});
            skLineSegment(sketch, "E975", {"start": v(11.89, -10.43) * mm, "end": v(11.98, -10.25) * mm});
            skLineSegment(sketch, "E976", {"start": v(11.98, -10.25) * mm, "end": v(13.37, -8.34) * mm});
            skLineSegment(sketch, "E977", {"start": v(13.37, -8.34) * mm, "end": v(13.51, -8.2) * mm});
            skLineSegment(sketch, "E978", {"start": v(13.51, -8.2) * mm, "end": v(13.7, -8.15) * mm});
            skLineSegment(sketch, "E979", {"start": v(13.7, -8.15) * mm, "end": v(13.9, -8.2) * mm});
            skLineSegment(sketch, "E980", {"start": v(13.9, -8.2) * mm, "end": v(15.67, -9.22) * mm});
            skLineSegment(sketch, "E981", {"start": v(15.67, -9.22) * mm, "end": v(16.05, -9.36) * mm});
            skLineSegment(sketch, "E982", {"start": v(16.05, -9.36) * mm, "end": v(16.71, -9.5) * mm});
            skLineSegment(sketch, "E983", {"start": v(16.71, -9.5) * mm, "end": v(17.65, -9.6) * mm});
            skLineSegment(sketch, "E984", {"start": v(17.65, -9.6) * mm, "end": v(18.85, -9.57) * mm});
            skLineSegment(sketch, "E985", {"start": v(18.85, -9.57) * mm, "end": v(19.68, -7.7) * mm});
            skLineSegment(sketch, "E986", {"start": v(2.37, 0) * mm, "end": v(2.35, 0.33) * mm});
            skLineSegment(sketch, "E987", {"start": v(2.35, 0.33) * mm, "end": v(2.29, 0.65) * mm});
            skLineSegment(sketch, "E988", {"start": v(2.29, 0.65) * mm, "end": v(2.18, 0.96) * mm});
            skLineSegment(sketch, "E989", {"start": v(2.18, 0.96) * mm, "end": v(2.04, 1.25) * mm});
            skLineSegment(sketch, "E990", {"start": v(2.04, 1.25) * mm, "end": v(1.86, 1.52) * mm});
            skLineSegment(sketch, "E991", {"start": v(1.86, 1.52) * mm, "end": v(1.64, 1.77) * mm});
            skLineSegment(sketch, "E992", {"start": v(1.64, 1.77) * mm, "end": v(1.4, 1.98) * mm});
            skLineSegment(sketch, "E993", {"start": v(1.4, 1.98) * mm, "end": v(1.12, 2.17) * mm});
            skLineSegment(sketch, "E994", {"start": v(1.12, 2.17) * mm, "end": v(0.83, 2.3) * mm});
            skLineSegment(sketch, "E995", {"start": v(0.83, 2.3) * mm, "end": v(0.52, 2.41) * mm});
            skLineSegment(sketch, "E996", {"start": v(0.52, 2.41) * mm, "end": v(0.2, 2.48) * mm});
            skLineSegment(sketch, "E997", {"start": v(0.2, 2.48) * mm, "end": v(-0.13, 2.5) * mm});
            skLineSegment(sketch, "E998", {"start": v(-0.13, 2.5) * mm, "end": v(-0.45, 2.48) * mm});
            skLineSegment(sketch, "E999", {"start": v(-0.45, 2.48) * mm, "end": v(-0.77, 2.41) * mm});
            skLineSegment(sketch, "E1000", {"start": v(-0.77, 2.41) * mm, "end": v(-1.08, 2.3) * mm});
            skLineSegment(sketch, "E1001", {"start": v(-1.08, 2.3) * mm, "end": v(-1.38, 2.17) * mm});
            skLineSegment(sketch, "E1002", {"start": v(-1.38, 2.17) * mm, "end": v(-1.65, 1.98) * mm});
            skLineSegment(sketch, "E1003", {"start": v(-1.65, 1.98) * mm, "end": v(-1.9, 1.77) * mm});
            skLineSegment(sketch, "E1004", {"start": v(-1.9, 1.77) * mm, "end": v(-2.1, 1.52) * mm});
            skLineSegment(sketch, "E1005", {"start": v(-2.1, 1.52) * mm, "end": v(-2.3, 1.25) * mm});
            skLineSegment(sketch, "E1006", {"start": v(-2.3, 1.25) * mm, "end": v(-2.43, 0.96) * mm});
            skLineSegment(sketch, "E1007", {"start": v(-2.43, 0.96) * mm, "end": v(-2.54, 0.65) * mm});
            skLineSegment(sketch, "E1008", {"start": v(-2.54, 0.65) * mm, "end": v(-2.6, 0.33) * mm});
            skLineSegment(sketch, "E1009", {"start": v(-2.6, 0.33) * mm, "end": v(-2.63, 0) * mm});
            skLineSegment(sketch, "E1010", {"start": v(-2.63, 0) * mm, "end": v(-2.6, -0.33) * mm});
            skLineSegment(sketch, "E1011", {"start": v(-2.6, -0.33) * mm, "end": v(-2.54, -0.65) * mm});
            skLineSegment(sketch, "E1012", {"start": v(-2.54, -0.65) * mm, "end": v(-2.43, -0.96) * mm});
            skLineSegment(sketch, "E1013", {"start": v(-2.43, -0.96) * mm, "end": v(-2.3, -1.25) * mm});
            skLineSegment(sketch, "E1014", {"start": v(-2.3, -1.25) * mm, "end": v(-2.1, -1.52) * mm});
            skLineSegment(sketch, "E1015", {"start": v(-2.1, -1.52) * mm, "end": v(-1.9, -1.77) * mm});
            skLineSegment(sketch, "E1016", {"start": v(-1.9, -1.77) * mm, "end": v(-1.65, -1.98) * mm});
            skLineSegment(sketch, "E1017", {"start": v(-1.65, -1.98) * mm, "end": v(-1.38, -2.17) * mm});
            skLineSegment(sketch, "E1018", {"start": v(-1.38, -2.17) * mm, "end": v(-1.08, -2.3) * mm});
            skLineSegment(sketch, "E1019", {"start": v(-1.08, -2.3) * mm, "end": v(-0.77, -2.41) * mm});
            skLineSegment(sketch, "E1020", {"start": v(-0.77, -2.41) * mm, "end": v(-0.45, -2.48) * mm});
            skLineSegment(sketch, "E1021", {"start": v(-0.45, -2.48) * mm, "end": v(-0.13, -2.5) * mm});
            skLineSegment(sketch, "E1022", {"start": v(-0.13, -2.5) * mm, "end": v(0.2, -2.48) * mm});
            skLineSegment(sketch, "E1023", {"start": v(0.2, -2.48) * mm, "end": v(0.52, -2.41) * mm});
            skLineSegment(sketch, "E1024", {"start": v(0.52, -2.41) * mm, "end": v(0.83, -2.3) * mm});
            skLineSegment(sketch, "E1025", {"start": v(0.83, -2.3) * mm, "end": v(1.12, -2.17) * mm});
            skLineSegment(sketch, "E1026", {"start": v(1.12, -2.17) * mm, "end": v(1.4, -1.98) * mm});
            skLineSegment(sketch, "E1027", {"start": v(1.4, -1.98) * mm, "end": v(1.64, -1.77) * mm});
            skLineSegment(sketch, "E1028", {"start": v(1.64, -1.77) * mm, "end": v(1.86, -1.52) * mm});
            skLineSegment(sketch, "E1029", {"start": v(1.86, -1.52) * mm, "end": v(2.04, -1.25) * mm});
            skLineSegment(sketch, "E1030", {"start": v(2.04, -1.25) * mm, "end": v(2.18, -0.96) * mm});
            skLineSegment(sketch, "E1031", {"start": v(2.18, -0.96) * mm, "end": v(2.29, -0.65) * mm});
            skLineSegment(sketch, "E1032", {"start": v(2.29, -0.65) * mm, "end": v(2.35, -0.33) * mm});
            skLineSegment(sketch, "E1033", {"start": v(2.35, -0.33) * mm, "end": v(2.37, 0) * mm});
            skSolve(sketch);
        }
        {
            var Q0;
            Q0 = qSketchRegion(id + "F6", true);
            extrude(context, id + "F7", {"entities" : qUnion([Q0]), "depth" : 4 * mm});
        }
        {
            var Q0;
            Q0=qCreatedBy(makeId("Front.planeOp"),FACE);
            var sketch = newSketch(context, id + "F8", { "sketchPlane" : qUnion([Q0])});
            skLineSegment(sketch, "E1034", {"start": v(15.62, -7.89) * mm, "end": v(15.33, -7.4) * mm});
            skLineSegment(sketch, "E1035", {"start": v(15.33, -7.4) * mm, "end": v(14.75, -6.6) * mm});
            skLineSegment(sketch, "E1036", {"start": v(14.75, -6.6) * mm, "end": v(14.23, -6.06) * mm});
            skLineSegment(sketch, "E1037", {"start": v(14.23, -6.06) * mm, "end": v(13.82, -5.7) * mm});
            skLineSegment(sketch, "E1038", {"start": v(13.82, -5.7) * mm, "end": v(13.54, -5.53) * mm});
            skLineSegment(sketch, "E1039", {"start": v(13.54, -5.53) * mm, "end": v(11.57, -4.72) * mm});
            skLineSegment(sketch, "E1040", {"start": v(11.57, -4.72) * mm, "end": v(11.41, -4.6) * mm});
            skLineSegment(sketch, "E1041", {"start": v(11.41, -4.6) * mm, "end": v(11.33, -4.4) * mm});
            skLineSegment(sketch, "E1042", {"start": v(11.33, -4.4) * mm, "end": v(11.36, -4.2) * mm});
            skLineSegment(sketch, "E1043", {"start": v(11.36, -4.2) * mm, "end": v(11.94, -2.04) * mm});
            skLineSegment(sketch, "E1044", {"start": v(11.94, -2.04) * mm, "end": v(12.02, -1.85) * mm});
            skLineSegment(sketch, "E1045", {"start": v(12.02, -1.85) * mm, "end": v(12.18, -1.73) * mm});
            skLineSegment(sketch, "E1046", {"start": v(12.18, -1.73) * mm, "end": v(12.38, -1.7) * mm});
            skLineSegment(sketch, "E1047", {"start": v(12.38, -1.7) * mm, "end": v(14.5, -1.98) * mm});
            skLineSegment(sketch, "E1048", {"start": v(14.5, -1.98) * mm, "end": v(14.82, -1.96) * mm});
            skLineSegment(sketch, "E1049", {"start": v(14.82, -1.96) * mm, "end": v(15.35, -1.87) * mm});
            skLineSegment(sketch, "E1050", {"start": v(15.35, -1.87) * mm, "end": v(16.08, -1.65) * mm});
            skLineSegment(sketch, "E1051", {"start": v(16.08, -1.65) * mm, "end": v(16.97, -1.26) * mm});
            skLineSegment(sketch, "E1052", {"start": v(16.97, -1.26) * mm, "end": v(17.47, -0.98) * mm});
            skLineSegment(sketch, "E1053", {"start": v(17.47, -0.98) * mm, "end": v(17.47, 0.98) * mm});
            skLineSegment(sketch, "E1054", {"start": v(17.47, 0.98) * mm, "end": v(16.97, 1.26) * mm});
            skLineSegment(sketch, "E1055", {"start": v(16.97, 1.26) * mm, "end": v(16.08, 1.65) * mm});
            skLineSegment(sketch, "E1056", {"start": v(16.08, 1.65) * mm, "end": v(15.35, 1.87) * mm});
            skLineSegment(sketch, "E1057", {"start": v(15.35, 1.87) * mm, "end": v(14.82, 1.96) * mm});
            skLineSegment(sketch, "E1058", {"start": v(14.82, 1.96) * mm, "end": v(14.5, 1.98) * mm});
            skLineSegment(sketch, "E1059", {"start": v(14.5, 1.98) * mm, "end": v(12.38, 1.7) * mm});
            skLineSegment(sketch, "E1060", {"start": v(12.38, 1.7) * mm, "end": v(12.18, 1.73) * mm});
            skLineSegment(sketch, "E1061", {"start": v(12.18, 1.73) * mm, "end": v(12.02, 1.85) * mm});
            skLineSegment(sketch, "E1062", {"start": v(12.02, 1.85) * mm, "end": v(11.94, 2.04) * mm});
            skLineSegment(sketch, "E1063", {"start": v(11.94, 2.04) * mm, "end": v(11.36, 4.2) * mm});
            skLineSegment(sketch, "E1064", {"start": v(11.36, 4.2) * mm, "end": v(11.33, 4.4) * mm});
            skLineSegment(sketch, "E1065", {"start": v(11.33, 4.4) * mm, "end": v(11.41, 4.6) * mm});
            skLineSegment(sketch, "E1066", {"start": v(11.41, 4.6) * mm, "end": v(11.57, 4.72) * mm});
            skLineSegment(sketch, "E1067", {"start": v(11.57, 4.72) * mm, "end": v(13.54, 5.53) * mm});
            skLineSegment(sketch, "E1068", {"start": v(13.54, 5.53) * mm, "end": v(13.82, 5.7) * mm});
            skLineSegment(sketch, "E1069", {"start": v(13.82, 5.7) * mm, "end": v(14.23, 6.06) * mm});
            skLineSegment(sketch, "E1070", {"start": v(14.23, 6.06) * mm, "end": v(14.75, 6.6) * mm});
            skLineSegment(sketch, "E1071", {"start": v(14.75, 6.6) * mm, "end": v(15.33, 7.4) * mm});
            skLineSegment(sketch, "E1072", {"start": v(15.33, 7.4) * mm, "end": v(15.62, 7.89) * mm});
            skLineSegment(sketch, "E1073", {"start": v(15.62, 7.89) * mm, "end": v(14.64, 9.58) * mm});
            skLineSegment(sketch, "E1074", {"start": v(14.64, 9.58) * mm, "end": v(14.07, 9.57) * mm});
            skLineSegment(sketch, "E1075", {"start": v(14.07, 9.57) * mm, "end": v(13.1, 9.47) * mm});
            skLineSegment(sketch, "E1076", {"start": v(13.1, 9.47) * mm, "end": v(12.36, 9.3) * mm});
            skLineSegment(sketch, "E1077", {"start": v(12.36, 9.3) * mm, "end": v(11.85, 9.11) * mm});
            skLineSegment(sketch, "E1078", {"start": v(11.85, 9.11) * mm, "end": v(11.56, 8.96) * mm});
            skLineSegment(sketch, "E1079", {"start": v(11.56, 8.96) * mm, "end": v(9.87, 7.66) * mm});
            skLineSegment(sketch, "E1080", {"start": v(9.87, 7.66) * mm, "end": v(9.69, 7.59) * mm});
            skLineSegment(sketch, "E1081", {"start": v(9.69, 7.59) * mm, "end": v(9.49, 7.61) * mm});
            skLineSegment(sketch, "E1082", {"start": v(9.49, 7.61) * mm, "end": v(9.32, 7.73) * mm});
            skLineSegment(sketch, "E1083", {"start": v(9.32, 7.73) * mm, "end": v(7.73, 9.32) * mm});
            skLineSegment(sketch, "E1084", {"start": v(7.73, 9.32) * mm, "end": v(7.61, 9.49) * mm});
            skLineSegment(sketch, "E1085", {"start": v(7.61, 9.49) * mm, "end": v(7.59, 9.69) * mm});
            skLineSegment(sketch, "E1086", {"start": v(7.59, 9.69) * mm, "end": v(7.66, 9.87) * mm});
            skLineSegment(sketch, "E1087", {"start": v(7.66, 9.87) * mm, "end": v(8.96, 11.56) * mm});
            skLineSegment(sketch, "E1088", {"start": v(8.96, 11.56) * mm, "end": v(9.11, 11.85) * mm});
            skLineSegment(sketch, "E1089", {"start": v(9.11, 11.85) * mm, "end": v(9.3, 12.36) * mm});
            skLineSegment(sketch, "E1090", {"start": v(9.3, 12.36) * mm, "end": v(9.47, 13.1) * mm});
            skLineSegment(sketch, "E1091", {"start": v(9.47, 13.1) * mm, "end": v(9.57, 14.07) * mm});
            skLineSegment(sketch, "E1092", {"start": v(9.57, 14.07) * mm, "end": v(9.58, 14.64) * mm});
            skLineSegment(sketch, "E1093", {"start": v(9.58, 14.64) * mm, "end": v(7.89, 15.62) * mm});
            skLineSegment(sketch, "E1094", {"start": v(7.89, 15.62) * mm, "end": v(7.4, 15.33) * mm});
            skLineSegment(sketch, "E1095", {"start": v(7.4, 15.33) * mm, "end": v(6.6, 14.75) * mm});
            skLineSegment(sketch, "E1096", {"start": v(6.6, 14.75) * mm, "end": v(6.06, 14.23) * mm});
            skLineSegment(sketch, "E1097", {"start": v(6.06, 14.23) * mm, "end": v(5.7, 13.82) * mm});
            skLineSegment(sketch, "E1098", {"start": v(5.7, 13.82) * mm, "end": v(5.53, 13.54) * mm});
            skLineSegment(sketch, "E1099", {"start": v(5.53, 13.54) * mm, "end": v(4.72, 11.57) * mm});
            skLineSegment(sketch, "E1100", {"start": v(4.72, 11.57) * mm, "end": v(4.6, 11.41) * mm});
            skLineSegment(sketch, "E1101", {"start": v(4.6, 11.41) * mm, "end": v(4.4, 11.33) * mm});
            skLineSegment(sketch, "E1102", {"start": v(4.4, 11.33) * mm, "end": v(4.2, 11.36) * mm});
            skLineSegment(sketch, "E1103", {"start": v(4.2, 11.36) * mm, "end": v(2.04, 11.94) * mm});
            skLineSegment(sketch, "E1104", {"start": v(2.04, 11.94) * mm, "end": v(1.85, 12.02) * mm});
            skLineSegment(sketch, "E1105", {"start": v(1.85, 12.02) * mm, "end": v(1.73, 12.18) * mm});
            skLineSegment(sketch, "E1106", {"start": v(1.73, 12.18) * mm, "end": v(1.7, 12.38) * mm});
            skLineSegment(sketch, "E1107", {"start": v(1.7, 12.38) * mm, "end": v(1.98, 14.5) * mm});
            skLineSegment(sketch, "E1108", {"start": v(1.98, 14.5) * mm, "end": v(1.96, 14.82) * mm});
            skLineSegment(sketch, "E1109", {"start": v(1.96, 14.82) * mm, "end": v(1.87, 15.35) * mm});
            skLineSegment(sketch, "E1110", {"start": v(1.87, 15.35) * mm, "end": v(1.65, 16.08) * mm});
            skLineSegment(sketch, "E1111", {"start": v(1.65, 16.08) * mm, "end": v(1.26, 16.97) * mm});
            skLineSegment(sketch, "E1112", {"start": v(1.26, 16.97) * mm, "end": v(0.98, 17.47) * mm});
            skLineSegment(sketch, "E1113", {"start": v(0.98, 17.47) * mm, "end": v(-0.98, 17.47) * mm});
            skLineSegment(sketch, "E1114", {"start": v(-0.98, 17.47) * mm, "end": v(-1.26, 16.97) * mm});
            skLineSegment(sketch, "E1115", {"start": v(-1.26, 16.97) * mm, "end": v(-1.65, 16.08) * mm});
            skLineSegment(sketch, "E1116", {"start": v(-1.65, 16.08) * mm, "end": v(-1.87, 15.35) * mm});
            skLineSegment(sketch, "E1117", {"start": v(-1.87, 15.35) * mm, "end": v(-1.96, 14.82) * mm});
            skLineSegment(sketch, "E1118", {"start": v(-1.96, 14.82) * mm, "end": v(-1.98, 14.5) * mm});
            skLineSegment(sketch, "E1119", {"start": v(-1.98, 14.5) * mm, "end": v(-1.7, 12.38) * mm});
            skLineSegment(sketch, "E1120", {"start": v(-1.7, 12.38) * mm, "end": v(-1.73, 12.18) * mm});
            skLineSegment(sketch, "E1121", {"start": v(-1.73, 12.18) * mm, "end": v(-1.85, 12.02) * mm});
            skLineSegment(sketch, "E1122", {"start": v(-1.85, 12.02) * mm, "end": v(-2.04, 11.94) * mm});
            skLineSegment(sketch, "E1123", {"start": v(-2.04, 11.94) * mm, "end": v(-4.2, 11.36) * mm});
            skLineSegment(sketch, "E1124", {"start": v(-4.2, 11.36) * mm, "end": v(-4.4, 11.33) * mm});
            skLineSegment(sketch, "E1125", {"start": v(-4.4, 11.33) * mm, "end": v(-4.6, 11.41) * mm});
            skLineSegment(sketch, "E1126", {"start": v(-4.6, 11.41) * mm, "end": v(-4.72, 11.57) * mm});
            skLineSegment(sketch, "E1127", {"start": v(-4.72, 11.57) * mm, "end": v(-5.53, 13.54) * mm});
            skLineSegment(sketch, "E1128", {"start": v(-5.53, 13.54) * mm, "end": v(-5.7, 13.82) * mm});
            skLineSegment(sketch, "E1129", {"start": v(-5.7, 13.82) * mm, "end": v(-6.06, 14.23) * mm});
            skLineSegment(sketch, "E1130", {"start": v(-6.06, 14.23) * mm, "end": v(-6.6, 14.75) * mm});
            skLineSegment(sketch, "E1131", {"start": v(-6.6, 14.75) * mm, "end": v(-7.4, 15.33) * mm});
            skLineSegment(sketch, "E1132", {"start": v(-7.4, 15.33) * mm, "end": v(-7.89, 15.62) * mm});
            skLineSegment(sketch, "E1133", {"start": v(-7.89, 15.62) * mm, "end": v(-9.58, 14.64) * mm});
            skLineSegment(sketch, "E1134", {"start": v(-9.58, 14.64) * mm, "end": v(-9.57, 14.07) * mm});
            skLineSegment(sketch, "E1135", {"start": v(-9.57, 14.07) * mm, "end": v(-9.47, 13.1) * mm});
            skLineSegment(sketch, "E1136", {"start": v(-9.47, 13.1) * mm, "end": v(-9.3, 12.36) * mm});
            skLineSegment(sketch, "E1137", {"start": v(-9.3, 12.36) * mm, "end": v(-9.11, 11.85) * mm});
            skLineSegment(sketch, "E1138", {"start": v(-9.11, 11.85) * mm, "end": v(-8.96, 11.56) * mm});
            skLineSegment(sketch, "E1139", {"start": v(-8.96, 11.56) * mm, "end": v(-7.66, 9.87) * mm});
            skLineSegment(sketch, "E1140", {"start": v(-7.66, 9.87) * mm, "end": v(-7.59, 9.69) * mm});
            skLineSegment(sketch, "E1141", {"start": v(-7.59, 9.69) * mm, "end": v(-7.61, 9.49) * mm});
            skLineSegment(sketch, "E1142", {"start": v(-7.61, 9.49) * mm, "end": v(-7.73, 9.32) * mm});
            skLineSegment(sketch, "E1143", {"start": v(-7.73, 9.32) * mm, "end": v(-9.32, 7.73) * mm});
            skLineSegment(sketch, "E1144", {"start": v(-9.32, 7.73) * mm, "end": v(-9.49, 7.61) * mm});
            skLineSegment(sketch, "E1145", {"start": v(-9.49, 7.61) * mm, "end": v(-9.69, 7.59) * mm});
            skLineSegment(sketch, "E1146", {"start": v(-9.69, 7.59) * mm, "end": v(-9.87, 7.66) * mm});
            skLineSegment(sketch, "E1147", {"start": v(-9.87, 7.66) * mm, "end": v(-11.56, 8.96) * mm});
            skLineSegment(sketch, "E1148", {"start": v(-11.56, 8.96) * mm, "end": v(-11.85, 9.11) * mm});
            skLineSegment(sketch, "E1149", {"start": v(-11.85, 9.11) * mm, "end": v(-12.36, 9.3) * mm});
            skLineSegment(sketch, "E1150", {"start": v(-12.36, 9.3) * mm, "end": v(-13.1, 9.47) * mm});
            skLineSegment(sketch, "E1151", {"start": v(-13.1, 9.47) * mm, "end": v(-14.07, 9.57) * mm});
            skLineSegment(sketch, "E1152", {"start": v(-14.07, 9.57) * mm, "end": v(-14.64, 9.58) * mm});
            skLineSegment(sketch, "E1153", {"start": v(-14.64, 9.58) * mm, "end": v(-15.62, 7.89) * mm});
            skLineSegment(sketch, "E1154", {"start": v(-15.62, 7.89) * mm, "end": v(-15.33, 7.4) * mm});
            skLineSegment(sketch, "E1155", {"start": v(-15.33, 7.4) * mm, "end": v(-14.75, 6.6) * mm});
            skLineSegment(sketch, "E1156", {"start": v(-14.75, 6.6) * mm, "end": v(-14.23, 6.06) * mm});
            skLineSegment(sketch, "E1157", {"start": v(-14.23, 6.06) * mm, "end": v(-13.82, 5.7) * mm});
            skLineSegment(sketch, "E1158", {"start": v(-13.82, 5.7) * mm, "end": v(-13.54, 5.53) * mm});
            skLineSegment(sketch, "E1159", {"start": v(-13.54, 5.53) * mm, "end": v(-11.57, 4.72) * mm});
            skLineSegment(sketch, "E1160", {"start": v(-11.57, 4.72) * mm, "end": v(-11.41, 4.6) * mm});
            skLineSegment(sketch, "E1161", {"start": v(-11.41, 4.6) * mm, "end": v(-11.33, 4.4) * mm});
            skLineSegment(sketch, "E1162", {"start": v(-11.33, 4.4) * mm, "end": v(-11.36, 4.2) * mm});
            skLineSegment(sketch, "E1163", {"start": v(-11.36, 4.2) * mm, "end": v(-11.94, 2.04) * mm});
            skLineSegment(sketch, "E1164", {"start": v(-11.94, 2.04) * mm, "end": v(-12.02, 1.85) * mm});
            skLineSegment(sketch, "E1165", {"start": v(-12.02, 1.85) * mm, "end": v(-12.18, 1.73) * mm});
            skLineSegment(sketch, "E1166", {"start": v(-12.18, 1.73) * mm, "end": v(-12.38, 1.7) * mm});
            skLineSegment(sketch, "E1167", {"start": v(-12.38, 1.7) * mm, "end": v(-14.5, 1.98) * mm});
            skLineSegment(sketch, "E1168", {"start": v(-14.5, 1.98) * mm, "end": v(-14.82, 1.96) * mm});
            skLineSegment(sketch, "E1169", {"start": v(-14.82, 1.96) * mm, "end": v(-15.35, 1.87) * mm});
            skLineSegment(sketch, "E1170", {"start": v(-15.35, 1.87) * mm, "end": v(-16.08, 1.65) * mm});
            skLineSegment(sketch, "E1171", {"start": v(-16.08, 1.65) * mm, "end": v(-16.97, 1.26) * mm});
            skLineSegment(sketch, "E1172", {"start": v(-16.97, 1.26) * mm, "end": v(-17.47, 0.98) * mm});
            skLineSegment(sketch, "E1173", {"start": v(-17.47, 0.98) * mm, "end": v(-17.47, -0.98) * mm});
            skLineSegment(sketch, "E1174", {"start": v(-17.47, -0.98) * mm, "end": v(-16.97, -1.26) * mm});
            skLineSegment(sketch, "E1175", {"start": v(-16.97, -1.26) * mm, "end": v(-16.08, -1.65) * mm});
            skLineSegment(sketch, "E1176", {"start": v(-16.08, -1.65) * mm, "end": v(-15.35, -1.87) * mm});
            skLineSegment(sketch, "E1177", {"start": v(-15.35, -1.87) * mm, "end": v(-14.82, -1.96) * mm});
            skLineSegment(sketch, "E1178", {"start": v(-14.82, -1.96) * mm, "end": v(-14.5, -1.98) * mm});
            skLineSegment(sketch, "E1179", {"start": v(-14.5, -1.98) * mm, "end": v(-12.38, -1.7) * mm});
            skLineSegment(sketch, "E1180", {"start": v(-12.38, -1.7) * mm, "end": v(-12.18, -1.73) * mm});
            skLineSegment(sketch, "E1181", {"start": v(-12.18, -1.73) * mm, "end": v(-12.02, -1.85) * mm});
            skLineSegment(sketch, "E1182", {"start": v(-12.02, -1.85) * mm, "end": v(-11.94, -2.04) * mm});
            skLineSegment(sketch, "E1183", {"start": v(-11.94, -2.04) * mm, "end": v(-11.36, -4.2) * mm});
            skLineSegment(sketch, "E1184", {"start": v(-11.36, -4.2) * mm, "end": v(-11.33, -4.4) * mm});
            skLineSegment(sketch, "E1185", {"start": v(-11.33, -4.4) * mm, "end": v(-11.41, -4.6) * mm});
            skLineSegment(sketch, "E1186", {"start": v(-11.41, -4.6) * mm, "end": v(-11.57, -4.72) * mm});
            skLineSegment(sketch, "E1187", {"start": v(-11.57, -4.72) * mm, "end": v(-13.54, -5.53) * mm});
            skLineSegment(sketch, "E1188", {"start": v(-13.54, -5.53) * mm, "end": v(-13.82, -5.7) * mm});
            skLineSegment(sketch, "E1189", {"start": v(-13.82, -5.7) * mm, "end": v(-14.23, -6.06) * mm});
            skLineSegment(sketch, "E1190", {"start": v(-14.23, -6.06) * mm, "end": v(-14.75, -6.6) * mm});
            skLineSegment(sketch, "E1191", {"start": v(-14.75, -6.6) * mm, "end": v(-15.33, -7.4) * mm});
            skLineSegment(sketch, "E1192", {"start": v(-15.33, -7.4) * mm, "end": v(-15.62, -7.89) * mm});
            skLineSegment(sketch, "E1193", {"start": v(-15.62, -7.89) * mm, "end": v(-14.64, -9.58) * mm});
            skLineSegment(sketch, "E1194", {"start": v(-14.64, -9.58) * mm, "end": v(-14.07, -9.57) * mm});
            skLineSegment(sketch, "E1195", {"start": v(-14.07, -9.57) * mm, "end": v(-13.1, -9.47) * mm});
            skLineSegment(sketch, "E1196", {"start": v(-13.1, -9.47) * mm, "end": v(-12.36, -9.3) * mm});
            skLineSegment(sketch, "E1197", {"start": v(-12.36, -9.3) * mm, "end": v(-11.85, -9.11) * mm});
            skLineSegment(sketch, "E1198", {"start": v(-11.85, -9.11) * mm, "end": v(-11.56, -8.96) * mm});
            skLineSegment(sketch, "E1199", {"start": v(-11.56, -8.96) * mm, "end": v(-9.87, -7.66) * mm});
            skLineSegment(sketch, "E1200", {"start": v(-9.87, -7.66) * mm, "end": v(-9.69, -7.59) * mm});
            skLineSegment(sketch, "E1201", {"start": v(-9.69, -7.59) * mm, "end": v(-9.49, -7.61) * mm});
            skLineSegment(sketch, "E1202", {"start": v(-9.49, -7.61) * mm, "end": v(-9.32, -7.73) * mm});
            skLineSegment(sketch, "E1203", {"start": v(-9.32, -7.73) * mm, "end": v(-7.73, -9.32) * mm});
            skLineSegment(sketch, "E1204", {"start": v(-7.73, -9.32) * mm, "end": v(-7.61, -9.49) * mm});
            skLineSegment(sketch, "E1205", {"start": v(-7.61, -9.49) * mm, "end": v(-7.59, -9.69) * mm});
            skLineSegment(sketch, "E1206", {"start": v(-7.59, -9.69) * mm, "end": v(-7.66, -9.87) * mm});
            skLineSegment(sketch, "E1207", {"start": v(-7.66, -9.87) * mm, "end": v(-8.96, -11.56) * mm});
            skLineSegment(sketch, "E1208", {"start": v(-8.96, -11.56) * mm, "end": v(-9.11, -11.85) * mm});
            skLineSegment(sketch, "E1209", {"start": v(-9.11, -11.85) * mm, "end": v(-9.3, -12.36) * mm});
            skLineSegment(sketch, "E1210", {"start": v(-9.3, -12.36) * mm, "end": v(-9.47, -13.1) * mm});
            skLineSegment(sketch, "E1211", {"start": v(-9.47, -13.1) * mm, "end": v(-9.57, -14.07) * mm});
            skLineSegment(sketch, "E1212", {"start": v(-9.57, -14.07) * mm, "end": v(-9.58, -14.64) * mm});
            skLineSegment(sketch, "E1213", {"start": v(-9.58, -14.64) * mm, "end": v(-7.89, -15.62) * mm});
            skLineSegment(sketch, "E1214", {"start": v(-7.89, -15.62) * mm, "end": v(-7.4, -15.33) * mm});
            skLineSegment(sketch, "E1215", {"start": v(-7.4, -15.33) * mm, "end": v(-6.6, -14.75) * mm});
            skLineSegment(sketch, "E1216", {"start": v(-6.6, -14.75) * mm, "end": v(-6.06, -14.23) * mm});
            skLineSegment(sketch, "E1217", {"start": v(-6.06, -14.23) * mm, "end": v(-5.7, -13.82) * mm});
            skLineSegment(sketch, "E1218", {"start": v(-5.7, -13.82) * mm, "end": v(-5.53, -13.54) * mm});
            skLineSegment(sketch, "E1219", {"start": v(-5.53, -13.54) * mm, "end": v(-4.72, -11.57) * mm});
            skLineSegment(sketch, "E1220", {"start": v(-4.72, -11.57) * mm, "end": v(-4.6, -11.41) * mm});
            skLineSegment(sketch, "E1221", {"start": v(-4.6, -11.41) * mm, "end": v(-4.4, -11.33) * mm});
            skLineSegment(sketch, "E1222", {"start": v(-4.4, -11.33) * mm, "end": v(-4.2, -11.36) * mm});
            skLineSegment(sketch, "E1223", {"start": v(-4.2, -11.36) * mm, "end": v(-2.04, -11.94) * mm});
            skLineSegment(sketch, "E1224", {"start": v(-2.04, -11.94) * mm, "end": v(-1.85, -12.02) * mm});
            skLineSegment(sketch, "E1225", {"start": v(-1.85, -12.02) * mm, "end": v(-1.73, -12.18) * mm});
            skLineSegment(sketch, "E1226", {"start": v(-1.73, -12.18) * mm, "end": v(-1.7, -12.38) * mm});
            skLineSegment(sketch, "E1227", {"start": v(-1.7, -12.38) * mm, "end": v(-1.98, -14.5) * mm});
            skLineSegment(sketch, "E1228", {"start": v(-1.98, -14.5) * mm, "end": v(-1.96, -14.82) * mm});
            skLineSegment(sketch, "E1229", {"start": v(-1.96, -14.82) * mm, "end": v(-1.87, -15.35) * mm});
            skLineSegment(sketch, "E1230", {"start": v(-1.87, -15.35) * mm, "end": v(-1.65, -16.08) * mm});
            skLineSegment(sketch, "E1231", {"start": v(-1.65, -16.08) * mm, "end": v(-1.26, -16.97) * mm});
            skLineSegment(sketch, "E1232", {"start": v(-1.26, -16.97) * mm, "end": v(-0.98, -17.47) * mm});
            skLineSegment(sketch, "E1233", {"start": v(-0.98, -17.47) * mm, "end": v(0.98, -17.47) * mm});
            skLineSegment(sketch, "E1234", {"start": v(0.98, -17.47) * mm, "end": v(1.26, -16.97) * mm});
            skLineSegment(sketch, "E1235", {"start": v(1.26, -16.97) * mm, "end": v(1.65, -16.08) * mm});
            skLineSegment(sketch, "E1236", {"start": v(1.65, -16.08) * mm, "end": v(1.87, -15.35) * mm});
            skLineSegment(sketch, "E1237", {"start": v(1.87, -15.35) * mm, "end": v(1.96, -14.82) * mm});
            skLineSegment(sketch, "E1238", {"start": v(1.96, -14.82) * mm, "end": v(1.98, -14.5) * mm});
            skLineSegment(sketch, "E1239", {"start": v(1.98, -14.5) * mm, "end": v(1.7, -12.38) * mm});
            skLineSegment(sketch, "E1240", {"start": v(1.7, -12.38) * mm, "end": v(1.73, -12.18) * mm});
            skLineSegment(sketch, "E1241", {"start": v(1.73, -12.18) * mm, "end": v(1.85, -12.02) * mm});
            skLineSegment(sketch, "E1242", {"start": v(1.85, -12.02) * mm, "end": v(2.04, -11.94) * mm});
            skLineSegment(sketch, "E1243", {"start": v(2.04, -11.94) * mm, "end": v(4.2, -11.36) * mm});
            skLineSegment(sketch, "E1244", {"start": v(4.2, -11.36) * mm, "end": v(4.4, -11.33) * mm});
            skLineSegment(sketch, "E1245", {"start": v(4.4, -11.33) * mm, "end": v(4.6, -11.41) * mm});
            skLineSegment(sketch, "E1246", {"start": v(4.6, -11.41) * mm, "end": v(4.72, -11.57) * mm});
            skLineSegment(sketch, "E1247", {"start": v(4.72, -11.57) * mm, "end": v(5.53, -13.54) * mm});
            skLineSegment(sketch, "E1248", {"start": v(5.53, -13.54) * mm, "end": v(5.7, -13.82) * mm});
            skLineSegment(sketch, "E1249", {"start": v(5.7, -13.82) * mm, "end": v(6.06, -14.23) * mm});
            skLineSegment(sketch, "E1250", {"start": v(6.06, -14.23) * mm, "end": v(6.6, -14.75) * mm});
            skLineSegment(sketch, "E1251", {"start": v(6.6, -14.75) * mm, "end": v(7.4, -15.33) * mm});
            skLineSegment(sketch, "E1252", {"start": v(7.4, -15.33) * mm, "end": v(7.89, -15.62) * mm});
            skLineSegment(sketch, "E1253", {"start": v(7.89, -15.62) * mm, "end": v(9.58, -14.64) * mm});
            skLineSegment(sketch, "E1254", {"start": v(9.58, -14.64) * mm, "end": v(9.57, -14.07) * mm});
            skLineSegment(sketch, "E1255", {"start": v(9.57, -14.07) * mm, "end": v(9.47, -13.1) * mm});
            skLineSegment(sketch, "E1256", {"start": v(9.47, -13.1) * mm, "end": v(9.3, -12.36) * mm});
            skLineSegment(sketch, "E1257", {"start": v(9.3, -12.36) * mm, "end": v(9.11, -11.85) * mm});
            skLineSegment(sketch, "E1258", {"start": v(9.11, -11.85) * mm, "end": v(8.96, -11.56) * mm});
            skLineSegment(sketch, "E1259", {"start": v(8.96, -11.56) * mm, "end": v(7.66, -9.87) * mm});
            skLineSegment(sketch, "E1260", {"start": v(7.66, -9.87) * mm, "end": v(7.59, -9.69) * mm});
            skLineSegment(sketch, "E1261", {"start": v(7.59, -9.69) * mm, "end": v(7.61, -9.49) * mm});
            skLineSegment(sketch, "E1262", {"start": v(7.61, -9.49) * mm, "end": v(7.73, -9.32) * mm});
            skLineSegment(sketch, "E1263", {"start": v(7.73, -9.32) * mm, "end": v(9.32, -7.73) * mm});
            skLineSegment(sketch, "E1264", {"start": v(9.32, -7.73) * mm, "end": v(9.49, -7.61) * mm});
            skLineSegment(sketch, "E1265", {"start": v(9.49, -7.61) * mm, "end": v(9.69, -7.59) * mm});
            skLineSegment(sketch, "E1266", {"start": v(9.69, -7.59) * mm, "end": v(9.87, -7.66) * mm});
            skLineSegment(sketch, "E1267", {"start": v(9.87, -7.66) * mm, "end": v(11.56, -8.96) * mm});
            skLineSegment(sketch, "E1268", {"start": v(11.56, -8.96) * mm, "end": v(11.85, -9.11) * mm});
            skLineSegment(sketch, "E1269", {"start": v(11.85, -9.11) * mm, "end": v(12.36, -9.3) * mm});
            skLineSegment(sketch, "E1270", {"start": v(12.36, -9.3) * mm, "end": v(13.1, -9.47) * mm});
            skLineSegment(sketch, "E1271", {"start": v(13.1, -9.47) * mm, "end": v(14.07, -9.57) * mm});
            skLineSegment(sketch, "E1272", {"start": v(14.07, -9.57) * mm, "end": v(14.64, -9.58) * mm});
            skLineSegment(sketch, "E1273", {"start": v(14.64, -9.58) * mm, "end": v(15.62, -7.89) * mm});
            skSolve(sketch);
        }
        {
            var Q0;
            Q0 = qSketchRegion(id + "F8", true);
            extrude(context, id + "F9", {"entities" : qUnion([Q0]), "depth" : 4 * mm});
        }
    });
